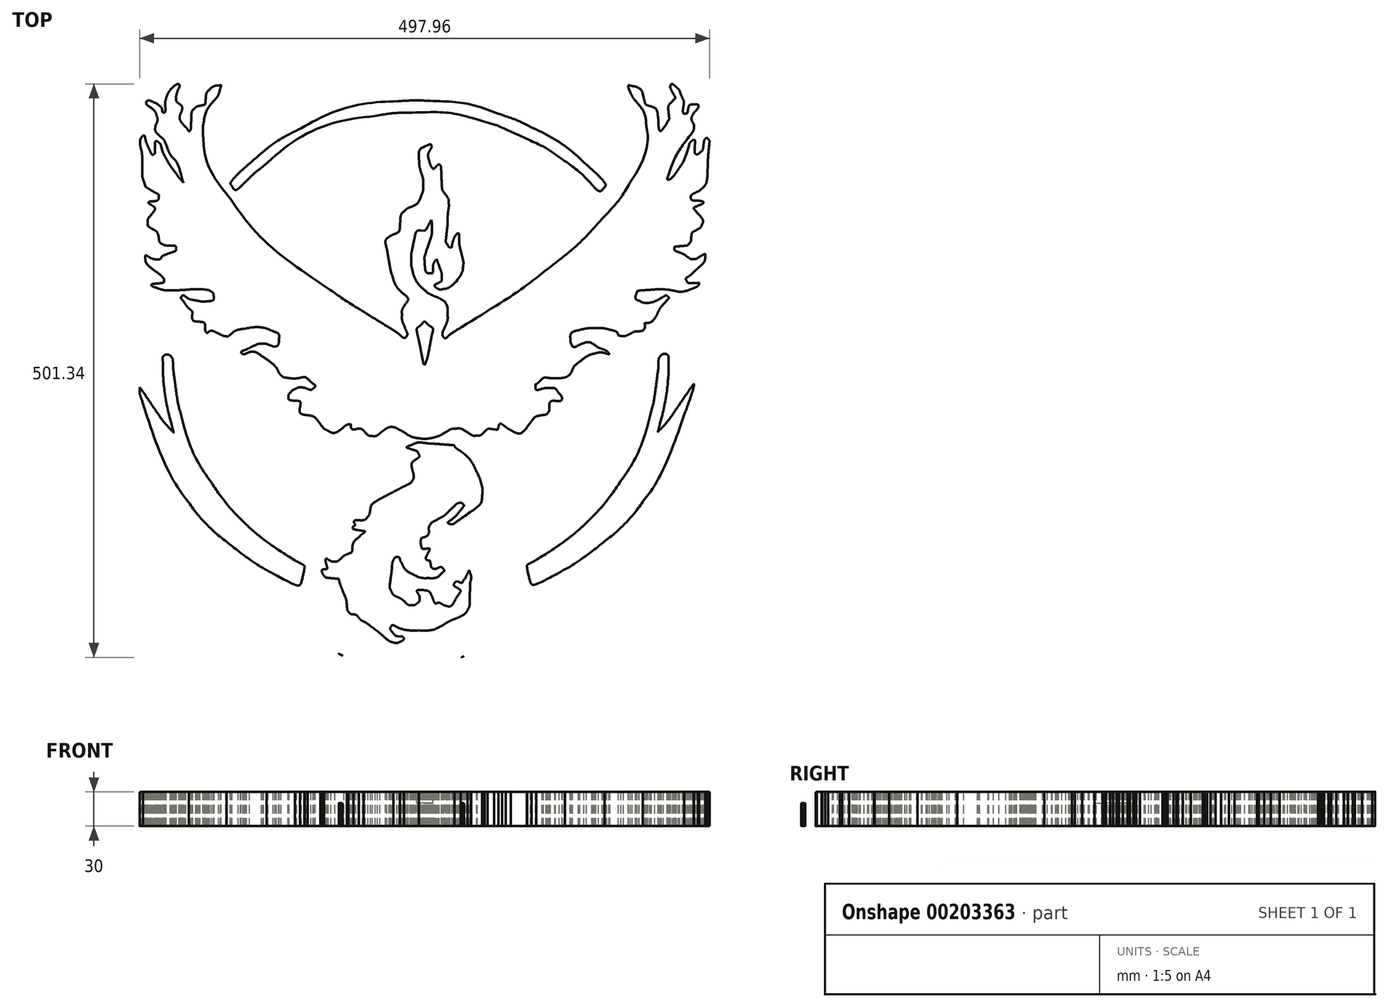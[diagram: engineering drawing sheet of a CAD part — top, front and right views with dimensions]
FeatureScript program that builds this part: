
annotation { "Feature Type Name" : "Feature", "Feature Type Description" : "" }
export const myFeature = defineFeature(function(context is Context, id is Id, definition is map)
    precondition{}
    {
        {
            var Q0;
            Q0=qCreatedBy(makeId("Top.planeOp"),FACE);
            var sketch = newSketch(context, id + "F0", { "sketchPlane" : qUnion([Q0])});
            skFitSpline(sketch, "E0", {"points": [v(217.87, 275.93) * mm, v(210.33, 275.93) * mm, v(203.9, 273.15) * mm, v(199.1, 269.63) * mm]});
            skFitSpline(sketch, "E1", {"points": [v(199.1, 269.63) * mm, v(196.14, 271.33) * mm, v(193.14, 272.64) * mm, v(190.27, 273.4) * mm]});
            skFitSpline(sketch, "E2", {"points": [v(190.27, 273.4) * mm, v(190.23, 273.4) * mm, v(190.19, 273.41) * mm, v(190.15, 273.42) * mm]});
            skFitSpline(sketch, "E3", {"points": [v(190.15, 273.42) * mm, v(188.24, 273.91) * mm, v(186.38, 274.47) * mm, v(182.33, 274.73) * mm]});
            skFitSpline(sketch, "E4", {"points": [v(182.33, 274.73) * mm, v(180.3, 274.85) * mm, v(177.7, 275.05) * mm, v(173.12, 274) * mm]});
            skFitSpline(sketch, "E5", {"points": [v(173.12, 274) * mm, v(168.53, 272.96) * mm, v(160.24, 269.98) * mm, v(154.3, 261.08) * mm]});
            skFitSpline(sketch, "E6", {"points": [v(154.3, 261.08) * mm, v(153.97, 260.58) * mm, v(153.65, 260.07) * mm, v(153.35, 259.54) * mm]});
            skFitSpline(sketch, "E7", {"points": [v(153.35, 259.54) * mm, v(145.44, 245.99) * mm, v(149.13, 243.88) * mm, v(149.3, 241.69) * mm]});
            skFitSpline(sketch, "E8", {"points": [v(149.3, 241.69) * mm, v(149.49, 239.5) * mm, v(149.72, 238.52) * mm, v(149.9, 237.7) * mm]});
            skFitSpline(sketch, "E9", {"points": [v(149.9, 237.7) * mm, v(150.24, 236.04) * mm, v(150.48, 235.27) * mm, v(150.7, 234.5) * mm]});
            skFitSpline(sketch, "E10", {"points": [v(150.7, 234.5) * mm, v(151.17, 232.95) * mm, v(151.58, 231.76) * mm, v(152.04, 230.48) * mm]});
            skFitSpline(sketch, "E11", {"points": [v(152.04, 230.48) * mm, v(152.95, 227.93) * mm, v(153.64, 225.9) * mm, v(155.43, 222.25) * mm]});
            skFitSpline(sketch, "E12", {"points": [v(155.43, 222.25) * mm, v(158.19, 216.6) * mm, v(159.29, 215.5) * mm, v(161.98, 212.21) * mm]});
            skFitSpline(sketch, "E13", {"points": [v(161.98, 212.21) * mm, v(165.62, 207.76) * mm, v(164.59, 210) * mm, v(165.02, 205.5) * mm]});
            skFitSpline(sketch, "E14", {"points": [v(165.02, 205.5) * mm, v(165.03, 205.48) * mm, v(165.03, 205.47) * mm, v(165.03, 205.45) * mm]});
            skFitSpline(sketch, "E15", {"points": [v(165.03, 205.45) * mm, v(165.05, 205.18) * mm, v(164.23, 200.38) * mm, v(162.5, 194.17) * mm]});
            skFitSpline(sketch, "E16", {"points": [v(162.5, 194.17) * mm, v(161.88, 194.74) * mm, v(161.27, 195.3) * mm, v(160.67, 195.83) * mm]});
            skLineSegment(sketch, "E17", {"start": v(160.67, 195.83) * mm, "end": v(160.66, 195.84) * mm});
            skFitSpline(sketch, "E18", {"points": [v(160.66, 195.84) * mm, v(144.48, 210.26) * mm, v(126.32, 222.5) * mm, v(106.6, 232.38) * mm]});
            skFitSpline(sketch, "E19", {"points": [v(106.6, 232.38) * mm, v(106.6, 232.39) * mm, v(106.59, 232.4) * mm, v(106.58, 232.4) * mm]});
            skFitSpline(sketch, "E20", {"points": [v(106.58, 232.4) * mm, v(96.35, 237.52) * mm, v(88.61, 240.69) * mm, v(74.93, 245.48) * mm]});
            skFitSpline(sketch, "E21", {"points": [v(74.93, 245.48) * mm, v(74.92, 245.48) * mm, v(74.91, 245.49) * mm, v(74.9, 245.5) * mm]});
            skFitSpline(sketch, "E22", {"points": [v(74.9, 245.5) * mm, v(53.44, 252.98) * mm, v(32.18, 256.93) * mm, v(7.67, 258.12) * mm]});
            skFitSpline(sketch, "E23", {"points": [v(7.67, 258.12) * mm, v(7.65, 258.13) * mm, v(7.63, 258.13) * mm, v(7.6, 258.13) * mm]});
            skFitSpline(sketch, "E24", {"points": [v(7.6, 258.13) * mm, v(5.3, 258.23) * mm, v(2.83, 258.3) * mm, v(0.2, 258.32) * mm]});
            skFitSpline(sketch, "E25", {"points": [v(0.2, 258.32) * mm, v(-7.68, 258.4) * mm, v(-16.55, 258.27) * mm, v(-23.41, 257.78) * mm]});
            skLineSegment(sketch, "E26", {"start": v(-23.41, 257.78) * mm, "end": v(-23.43, 257.77) * mm});
            skFitSpline(sketch, "E27", {"points": [v(-23.43, 257.77) * mm, v(-56.56, 255.36) * mm, v(-89.54, 246.17) * mm, v(-118.8, 231.18) * mm]});
            skLineSegment(sketch, "E28", {"start": v(-118.8, 231.18) * mm, "end": v(-118.8, 231.17) * mm});
            skFitSpline(sketch, "E29", {"points": [v(-118.8, 231.17) * mm, v(-133.83, 223.46) * mm, v(-147.06, 214.76) * mm, v(-161.5, 203.13) * mm]});
            skFitSpline(sketch, "E30", {"points": [v(-161.5, 203.13) * mm, v(-161.4, 204.67) * mm, v(-161.33, 207.22) * mm, v(-161.45, 207.37) * mm]});
            skFitSpline(sketch, "E31", {"points": [v(-161.45, 207.37) * mm, v(-161.13, 208.45) * mm, v(-160.13, 210.7) * mm, v(-158.87, 212.2) * mm]});
            skLineSegment(sketch, "E32", {"start": v(-158.87, 212.2) * mm, "end": v(-159.02, 212.01) * mm});
            skFitSpline(sketch, "E33", {"points": [v(-159.02, 212.01) * mm, v(-154.46, 217.33) * mm, v(-149.72, 226.82) * mm, v(-147.9, 233.25) * mm]});
            skLineSegment(sketch, "E34", {"start": v(-147.9, 233.25) * mm, "end": v(-147.96, 233.06) * mm});
            skFitSpline(sketch, "E35", {"points": [v(-147.96, 233.06) * mm, v(-147.66, 234.1) * mm, v(-147.23, 235.27) * mm, v(-146.73, 238.35) * mm]});
            skFitSpline(sketch, "E36", {"points": [v(-146.73, 238.35) * mm, v(-146.23, 241.42) * mm, v(-144.3, 248.07) * mm, v(-150.13, 258.68) * mm]});
            skFitSpline(sketch, "E37", {"points": [v(-150.13, 258.68) * mm, v(-155.95, 269.3) * mm, v(-168.74, 273.93) * mm, v(-173.7, 274.53) * mm]});
            skFitSpline(sketch, "E38", {"points": [v(-173.7, 274.53) * mm, v(-178.67, 275.13) * mm, v(-180.16, 274.7) * mm, v(-181.26, 274.6) * mm]});
            skLineSegment(sketch, "E39", {"start": v(-181.26, 274.6) * mm, "end": v(-181.03, 274.63) * mm});
            skFitSpline(sketch, "E40", {"points": [v(-181.03, 274.63) * mm, v(-188.08, 274.08) * mm, v(-192.97, 272.73) * mm, v(-197.12, 270.53) * mm]});
            skFitSpline(sketch, "E41", {"points": [v(-197.12, 270.53) * mm, v(-198.09, 271.18) * mm, v(-199.07, 271.78) * mm, v(-200.1, 272.3) * mm]});
            skFitSpline(sketch, "E42", {"points": [v(-200.1, 272.3) * mm, v(-210.4, 277.41) * mm, v(-221.7, 276.07) * mm, v(-229.74, 271.82) * mm]});
            skFitSpline(sketch, "E43", {"points": [v(-229.74, 271.82) * mm, v(-229.8, 271.78) * mm, v(-229.87, 271.75) * mm, v(-229.93, 271.72) * mm]});
            skFitSpline(sketch, "E44", {"points": [v(-229.93, 271.72) * mm, v(-238.87, 266.9) * mm, v(-236.88, 266.92) * mm, v(-238.75, 265.23) * mm]});
            skFitSpline(sketch, "E45", {"points": [v(-238.75, 265.23) * mm, v(-240.22, 263.9) * mm, v(-240.43, 264.86) * mm, v(-243.28, 261.1) * mm]});
            skFitSpline(sketch, "E46", {"points": [v(-243.28, 261.1) * mm, v(-249.02, 260.28) * mm, v(-254.1, 257.93) * mm, v(-258.33, 254.82) * mm]});
            skFitSpline(sketch, "E47", {"points": [v(-258.33, 254.82) * mm, v(-266.03, 249.14) * mm, v(-274.63, 236.82) * mm, v(-270.76, 221.05) * mm]});
            skFitSpline(sketch, "E48", {"points": [v(-270.76, 221.05) * mm, v(-270.7, 220.86) * mm, v(-270.66, 220.66) * mm, v(-270.6, 220.47) * mm]});
            skFitSpline(sketch, "E49", {"points": [v(-270.6, 220.47) * mm, v(-270.33, 219.42) * mm, v(-270.04, 218.5) * mm, v(-269.76, 217.62) * mm]});
            skFitSpline(sketch, "E50", {"points": [v(-269.76, 217.62) * mm, v(-270.53, 216.6) * mm, v(-271.32, 215.43) * mm, v(-272.15, 214.06) * mm]});
            skFitSpline(sketch, "E51", {"points": [v(-272.15, 214.06) * mm, v(-272.16, 214.04) * mm, v(-272.17, 214.03) * mm, v(-272.18, 214) * mm]});
            skFitSpline(sketch, "E52", {"points": [v(-272.18, 214) * mm, v(-273.24, 212.26) * mm, v(-276, 206.15) * mm, v(-276.7, 201.8) * mm]});
            skFitSpline(sketch, "E53", {"points": [v(-276.7, 201.8) * mm, v(-277.38, 197.68) * mm, v(-277.22, 195.9) * mm, v(-277.2, 194.35) * mm]});
            skFitSpline(sketch, "E54", {"points": [v(-277.2, 194.35) * mm, v(-277.2, 190.35) * mm, v(-277.76, 189.7) * mm, v(-275.74, 182.22) * mm]});
            skFitSpline(sketch, "E55", {"points": [v(-275.74, 182.22) * mm, v(-275.35, 180.83) * mm, v(-275.57, 182.83) * mm, v(-275.52, 174.9) * mm]});
            skFitSpline(sketch, "E56", {"points": [v(-275.52, 174.9) * mm, v(-275.52, 174.9) * mm, v(-275.52, 174.9) * mm, v(-275.52, 174.9) * mm]});
            skFitSpline(sketch, "E57", {"points": [v(-275.52, 174.9) * mm, v(-275.47, 165) * mm, v(-273.97, 155.5) * mm, v(-271.7, 148.63) * mm]});
            skFitSpline(sketch, "E58", {"points": [v(-271.7, 148.63) * mm, v(-271.7, 148.62) * mm, v(-271.69, 148.6) * mm, v(-271.68, 148.59) * mm]});
            skLineSegment(sketch, "E59", {"start": v(-271.68, 148.59) * mm, "end": v(-270.9, 146.22) * mm});
            skFitSpline(sketch, "E60", {"points": [v(-270.9, 146.22) * mm, v(-270.55, 145.2) * mm, v(-270.15, 144.2) * mm, v(-269.7, 143.21) * mm]});
            skFitSpline(sketch, "E61", {"points": [v(-269.7, 143.21) * mm, v(-269.7, 142.96) * mm, v(-269.75, 142.7) * mm, v(-269.76, 142.45) * mm]});
            skFitSpline(sketch, "E62", {"points": [v(-269.76, 142.45) * mm, v(-269.78, 139.72) * mm, v(-269.44, 137.28) * mm, v(-268.92, 135.06) * mm]});
            skFitSpline(sketch, "E63", {"points": [v(-268.92, 135.06) * mm, v(-269.93, 131.8) * mm, v(-270.61, 128.35) * mm, v(-270.61, 124.93) * mm]});
            skFitSpline(sketch, "E64", {"points": [v(-270.61, 124.93) * mm, v(-270.61, 121.34) * mm, v(-269.53, 116.12) * mm, v(-267.6, 111.19) * mm]});
            skFitSpline(sketch, "E65", {"points": [v(-267.6, 111.19) * mm, v(-270.75, 106.2) * mm, v(-272, 101.24) * mm, v(-272.4, 98.4) * mm]});
            skFitSpline(sketch, "E66", {"points": [v(-272.4, 98.4) * mm, v(-273.06, 93.69) * mm, v(-272.73, 91.52) * mm, v(-272.57, 89.72) * mm]});
            skFitSpline(sketch, "E67", {"points": [v(-272.57, 89.72) * mm, v(-272.46, 88.32) * mm, v(-272.53, 86.77) * mm, v(-271.34, 82.44) * mm]});
            skFitSpline(sketch, "E68", {"points": [v(-271.34, 82.44) * mm, v(-271.15, 81.75) * mm, v(-270.82, 80.9) * mm, v(-270.43, 79.97) * mm]});
            skFitSpline(sketch, "E69", {"points": [v(-270.43, 79.97) * mm, v(-270.58, 80.56) * mm, v(-270.71, 81.2) * mm, v(-270.84, 81.87) * mm]});
            skFitSpline(sketch, "E70", {"points": [v(-270.84, 81.87) * mm, v(-270.67, 81.04) * mm, v(-270.49, 80.3) * mm, v(-270.28, 79.64) * mm]});
            skFitSpline(sketch, "E71", {"points": [v(-270.28, 79.64) * mm, v(-269.43, 77.72) * mm, v(-268.23, 75.47) * mm, v(-266.65, 73.17) * mm]});
            skFitSpline(sketch, "E72", {"points": [v(-266.65, 73.17) * mm, v(-266.67, 73.06) * mm, v(-266.7, 72.94) * mm, v(-266.71, 72.82) * mm]});
            skFitSpline(sketch, "E73", {"points": [v(-266.71, 72.82) * mm, v(-266.3, 72.18) * mm, v(-265.94, 71.61) * mm, v(-265.64, 71.2) * mm]});
            skFitSpline(sketch, "E74", {"points": [v(-265.64, 71.2) * mm, v(-266.01, 71.6) * mm, v(-266.34, 71.97) * mm, v(-266.76, 72.47) * mm]});
            skFitSpline(sketch, "E75", {"points": [v(-266.76, 72.47) * mm, v(-267.02, 70.24) * mm, v(-267.04, 68.13) * mm, v(-266.78, 66.3) * mm]});
            skFitSpline(sketch, "E76", {"points": [v(-266.78, 66.3) * mm, v(-265.72, 58.82) * mm, v(-263.1, 55.2) * mm, v(-261.37, 52.78) * mm]});
            skFitSpline(sketch, "E77", {"points": [v(-261.37, 52.78) * mm, v(-257.92, 47.93) * mm, v(-256.07, 46.94) * mm, v(-254.59, 45.8) * mm]});
            skFitSpline(sketch, "E78", {"points": [v(-254.59, 45.8) * mm, v(-251.62, 43.52) * mm, v(-249.98, 42.7) * mm, v(-248.16, 41.75) * mm]});
            skFitSpline(sketch, "E79", {"points": [v(-248.16, 41.75) * mm, v(-245.76, 40.47) * mm, v(-243.56, 39.39) * mm, v(-240.8, 38.37) * mm]});
            skFitSpline(sketch, "E80", {"points": [v(-240.8, 38.37) * mm, v(-243.17, 37.13) * mm, v(-245.64, 35.49) * mm, v(-248.19, 33.3) * mm]});
            skLineSegment(sketch, "E81", {"start": v(-248.19, 33.3) * mm, "end": v(-248.98, 32.63) * mm});
            skFitSpline(sketch, "E82", {"points": [v(-248.98, 32.63) * mm, v(-255.3, 27.19) * mm, v(-259.37, 19.58) * mm, v(-260.38, 11.3) * mm]});
            skFitSpline(sketch, "E83", {"points": [v(-260.38, 11.3) * mm, v(-272.63, 6.13) * mm, v(-280.65, -5.81) * mm, v(-280.82, -19.11) * mm]});
            skLineSegment(sketch, "E84", {"start": v(-280.82, -19.11) * mm, "end": v(-280.84, -21.46) * mm});
            skFitSpline(sketch, "E85", {"points": [v(-280.84, -21.46) * mm, v(-280.84, -21.59) * mm, v(-280.85, -21.72) * mm, v(-280.85, -21.86) * mm]});
            skFitSpline(sketch, "E86", {"points": [v(-280.85, -21.86) * mm, v(-280.85, -24.72) * mm, v(-280.29, -30.22) * mm, v(-279.37, -33.94) * mm]});
            skFitSpline(sketch, "E87", {"points": [v(-279.37, -33.94) * mm, v(-278.45, -37.67) * mm, v(-277.52, -40.33) * mm, v(-276.2, -44.28) * mm]});
            skFitSpline(sketch, "E88", {"points": [v(-276.2, -44.28) * mm, v(-276.19, -44.3) * mm, v(-276.18, -44.33) * mm, v(-276.17, -44.35) * mm]});
            skFitSpline(sketch, "E89", {"points": [v(-276.17, -44.35) * mm, v(-263.73, -81.15) * mm, v(-248.31, -116.35) * mm, v(-231.6, -139.58) * mm]});
            skFitSpline(sketch, "E90", {"points": [v(-231.6, -139.58) * mm, v(-231.6, -139.59) * mm, v(-231.6, -139.59) * mm, v(-231.6, -139.59) * mm]});
            skFitSpline(sketch, "E91", {"points": [v(-231.6, -139.59) * mm, v(-231.59, -139.6) * mm, v(-231.59, -139.6) * mm, v(-231.59, -139.6) * mm]});
            skFitSpline(sketch, "E92", {"points": [v(-231.59, -139.6) * mm, v(-221.07, -154.22) * mm, v(-206.57, -169.11) * mm, v(-192.24, -180.57) * mm]});
            skFitSpline(sketch, "E93", {"points": [v(-192.24, -180.57) * mm, v(-180.15, -190.28) * mm, v(-165.88, -201.17) * mm, v(-152.64, -208.47) * mm]});
            skFitSpline(sketch, "E94", {"points": [v(-152.64, -208.47) * mm, v(-147.53, -211.3) * mm, v(-141.76, -214.36) * mm, v(-136.76, -216.94) * mm]});
            skFitSpline(sketch, "E95", {"points": [v(-136.76, -216.94) * mm, v(-131.75, -219.52) * mm, v(-131.21, -220.35) * mm, v(-123.5, -223.28) * mm]});
            skFitSpline(sketch, "E96", {"points": [v(-123.5, -223.28) * mm, v(-123.3, -223.35) * mm, v(-123.09, -223.43) * mm, v(-122.88, -223.5) * mm]});
            skFitSpline(sketch, "E97", {"points": [v(-122.88, -223.5) * mm, v(-117.12, -225.56) * mm, v(-113.06, -226) * mm, v(-107.92, -225.81) * mm]});
            skFitSpline(sketch, "E98", {"points": [v(-107.92, -225.81) * mm, v(-105.13, -225.72) * mm, v(-101.73, -226.74) * mm, v(-97.05, -225.24) * mm]});
            skFitSpline(sketch, "E99", {"points": [v(-97.05, -225.24) * mm, v(-95.61, -228.87) * mm, v(-93.44, -232.84) * mm, v(-92.3, -234.5) * mm]});
            skFitSpline(sketch, "E100", {"points": [v(-92.3, -234.5) * mm, v(-88, -240.63) * mm, v(-81.93, -245.22) * mm, v(-75.36, -248.02) * mm]});
            skFitSpline(sketch, "E101", {"points": [v(-75.36, -248.02) * mm, v(-72.71, -250.18) * mm, v(-69.9, -252.2) * mm, v(-67.81, -253.33) * mm]});
            skLineSegment(sketch, "E102", {"start": v(-67.81, -253.33) * mm, "end": v(-68.16, -253.13) * mm});
            skFitSpline(sketch, "E103", {"points": [v(-68.16, -253.13) * mm, v(-71.04, -251.52) * mm, v(-67, -253.96) * mm, v(-64.22, -256.03) * mm]});
            skFitSpline(sketch, "E104", {"points": [v(-64.22, -256.03) * mm, v(-61.44, -258.1) * mm, v(-58.17, -260.68) * mm, v(-56.25, -262.3) * mm]});
            skFitSpline(sketch, "E105", {"points": [v(-56.25, -262.3) * mm, v(-56.22, -262.33) * mm, v(-56.2, -262.35) * mm, v(-56.17, -262.37) * mm]});
            skFitSpline(sketch, "E106", {"points": [v(-56.17, -262.37) * mm, v(-50.78, -266.9) * mm, v(-44.46, -271.73) * mm, v(-35, -274.45) * mm]});
            skFitSpline(sketch, "E107", {"points": [v(-35, -274.45) * mm, v(-34.87, -274.49) * mm, v(-34.75, -274.52) * mm, v(-34.63, -274.55) * mm]});
            skFitSpline(sketch, "E108", {"points": [v(-34.63, -274.55) * mm, v(-25.12, -277.17) * mm, v(-13.96, -275.95) * mm, v(-5.5, -271.85) * mm]});
            skFitSpline(sketch, "E109", {"points": [v(-5.5, -271.85) * mm, v(-5.47, -271.83) * mm, v(-5.43, -271.82) * mm, v(-5.4, -271.8) * mm]});
            skFitSpline(sketch, "E110", {"points": [v(-5.4, -271.8) * mm, v(-2.1, -270.2) * mm, v(1.53, -268.22) * mm, v(5.15, -264.63) * mm]});
            skFitSpline(sketch, "E111", {"points": [v(5.15, -264.63) * mm, v(16.55, -263.22) * mm, v(28.3, -259.27) * mm, v(37.99, -253.78) * mm]});
            skFitSpline(sketch, "E112", {"points": [v(37.99, -253.78) * mm, v(38.05, -253.75) * mm, v(38.1, -253.72) * mm, v(38.16, -253.69) * mm]});
            skFitSpline(sketch, "E113", {"points": [v(38.16, -253.69) * mm, v(36.19, -254.82) * mm, v(39.56, -253.09) * mm, v(39.86, -252.97) * mm]});
            skFitSpline(sketch, "E114", {"points": [v(39.86, -252.97) * mm, v(39.94, -252.94) * mm, v(40.01, -252.9) * mm, v(40.09, -252.88) * mm]});
            skFitSpline(sketch, "E115", {"points": [v(40.09, -252.88) * mm, v(42.8, -251.78) * mm, v(44.12, -251.38) * mm, v(48.26, -249.25) * mm]});
            skFitSpline(sketch, "E116", {"points": [v(48.26, -249.25) * mm, v(48.43, -249.16) * mm, v(48.6, -249.07) * mm, v(48.77, -248.98) * mm]});
            skFitSpline(sketch, "E117", {"points": [v(48.77, -248.98) * mm, v(59.28, -243.33) * mm, v(61.39, -243.75) * mm, v(68.93, -228.65) * mm]});
            skFitSpline(sketch, "E118", {"points": [v(68.93, -228.65) * mm, v(68.95, -228.61) * mm, v(68.97, -228.58) * mm, v(68.99, -228.54) * mm]});
            skFitSpline(sketch, "E119", {"points": [v(68.99, -228.54) * mm, v(69.56, -227.39) * mm, v(70.4, -225.32) * mm, v(71.21, -222.93) * mm]});
            skFitSpline(sketch, "E120", {"points": [v(71.21, -222.93) * mm, v(82.19, -232.42) * mm, v(89.6, -230.78) * mm, v(95, -231) * mm]});
            skFitSpline(sketch, "E121", {"points": [v(95, -231) * mm, v(101.2, -231.25) * mm, v(106.18, -230.53) * mm, v(112.23, -228.38) * mm]});
            skFitSpline(sketch, "E122", {"points": [v(112.23, -228.38) * mm, v(122.6, -224.7) * mm, v(121.63, -224.23) * mm, v(126.71, -221.62) * mm]});
            skFitSpline(sketch, "E123", {"points": [v(126.71, -221.62) * mm, v(131.78, -219.02) * mm, v(137.62, -215.92) * mm, v(142.99, -212.93) * mm]});
            skFitSpline(sketch, "E124", {"points": [v(142.99, -212.93) * mm, v(157.44, -204.97) * mm, v(170.99, -194.47) * mm, v(183.37, -184.52) * mm]});
            skLineSegment(sketch, "E125", {"start": v(183.37, -184.52) * mm, "end": v(183.38, -184.51) * mm});
            skFitSpline(sketch, "E126", {"points": [v(183.38, -184.51) * mm, v(198.33, -172.57) * mm, v(212.77, -157.77) * mm, v(223.83, -142.38) * mm]});
            skLineSegment(sketch, "E127", {"start": v(223.83, -142.38) * mm, "end": v(223.83, -142.37) * mm});
            skFitSpline(sketch, "E128", {"points": [v(223.83, -142.37) * mm, v(239.27, -120.92) * mm, v(252.53, -91.56) * mm, v(265.2, -56.84) * mm]});
            skFitSpline(sketch, "E129", {"points": [v(265.2, -56.84) * mm, v(266.9, -52.25) * mm, v(268.81, -46.69) * mm, v(270.5, -41.64) * mm]});
            skFitSpline(sketch, "E130", {"points": [v(270.5, -41.64) * mm, v(272.18, -36.6) * mm, v(272.84, -35.82) * mm, v(274.65, -28.1) * mm]});
            skFitSpline(sketch, "E131", {"points": [v(274.65, -28.1) * mm, v(275.08, -26.25) * mm, v(275.57, -24.23) * mm, v(275.82, -20.38) * mm]});
            skFitSpline(sketch, "E132", {"points": [v(275.82, -20.38) * mm, v(276.06, -16.52) * mm, v(279.73, -10.63) * mm, v(268.82, 5.1) * mm]});
            skFitSpline(sketch, "E133", {"points": [v(268.82, 5.1) * mm, v(265.57, 9.79) * mm, v(259.42, 14.66) * mm, v(252.6, 17.97) * mm]});
            skFitSpline(sketch, "E134", {"points": [v(252.6, 17.97) * mm, v(250.66, 25.14) * mm, v(246.73, 31.6) * mm, v(241.27, 36.63) * mm]});
            skFitSpline(sketch, "E135", {"points": [v(241.27, 36.63) * mm, v(243.76, 37.45) * mm, v(244.12, 38.02) * mm, v(246.2, 38.87) * mm]});
            skFitSpline(sketch, "E136", {"points": [v(246.2, 38.87) * mm, v(247.84, 39.54) * mm, v(249.4, 40.2) * mm, v(250.98, 40.92) * mm]});
            skFitSpline(sketch, "E137", {"points": [v(250.98, 40.92) * mm, v(251.77, 41.28) * mm, v(252.54, 41.63) * mm, v(253.6, 42.18) * mm]});
            skFitSpline(sketch, "E138", {"points": [v(253.6, 42.18) * mm, v(254.65, 42.73) * mm, v(254.5, 41.5) * mm, v(260.54, 46.9) * mm]});
            skFitSpline(sketch, "E139", {"points": [v(260.54, 46.9) * mm, v(260.63, 46.97) * mm, v(260.7, 47.05) * mm, v(260.8, 47.12) * mm]});
            skFitSpline(sketch, "E140", {"points": [v(260.8, 47.12) * mm, v(272, 57.35) * mm, v(270.53, 62) * mm, v(271.1, 68.08) * mm]});
            skFitSpline(sketch, "E141", {"points": [v(271.1, 68.08) * mm, v(271.3, 70.16) * mm, v(271.7, 72.28) * mm, v(271.07, 75.85) * mm]});
            skFitSpline(sketch, "E142", {"points": [v(271.07, 75.85) * mm, v(273.94, 80.9) * mm, v(276.16, 86.45) * mm, v(276.77, 91.59) * mm]});
            skFitSpline(sketch, "E143", {"points": [v(276.77, 91.59) * mm, v(276.8, 91.75) * mm, v(276.81, 91.91) * mm, v(276.83, 92.08) * mm]});
            skFitSpline(sketch, "E144", {"points": [v(276.83, 92.08) * mm, v(276.95, 93.26) * mm, v(277.5, 94.24) * mm, v(276.87, 99.91) * mm]});
            skFitSpline(sketch, "E145", {"points": [v(276.87, 99.91) * mm, v(276.56, 102.68) * mm, v(275.88, 107.27) * mm, v(272.37, 112.9) * mm]});
            skFitSpline(sketch, "E146", {"points": [v(272.37, 112.9) * mm, v(274.35, 118.62) * mm, v(274.75, 126.19) * mm, v(273.6, 132.52) * mm]});
            skFitSpline(sketch, "E147", {"points": [v(273.6, 132.52) * mm, v(274.65, 135.5) * mm, v(275.48, 139.34) * mm, v(275.2, 144.23) * mm]});
            skFitSpline(sketch, "E148", {"points": [v(275.2, 144.23) * mm, v(275.14, 145.24) * mm, v(274.99, 146.29) * mm, v(274.8, 147.35) * mm]});
            skFitSpline(sketch, "E149", {"points": [v(274.8, 147.35) * mm, v(276.38, 150.78) * mm, v(277.6, 154.34) * mm, v(278.1, 157.63) * mm]});
            skFitSpline(sketch, "E150", {"points": [v(278.1, 157.63) * mm, v(278.87, 162.38) * mm, v(278.6, 162.25) * mm, v(278.73, 164.32) * mm]});
            skFitSpline(sketch, "E151", {"points": [v(278.73, 164.32) * mm, v(278.85, 166.43) * mm, v(278.96, 168.85) * mm, v(279.05, 171.29) * mm]});
            skLineSegment(sketch, "E152", {"start": v(279.05, 171.29) * mm, "end": v(279.05, 171.32) * mm});
            skFitSpline(sketch, "E153", {"points": [v(279.05, 171.32) * mm, v(279.32, 178.6) * mm, v(279.64, 183.28) * mm, v(280.33, 189.62) * mm]});
            skLineSegment(sketch, "E154", {"start": v(280.33, 189.62) * mm, "end": v(280.33, 189.64) * mm});
            skLineSegment(sketch, "E155", {"start": v(280.33, 189.64) * mm, "end": v(280.66, 192.55) * mm});
            skFitSpline(sketch, "E156", {"points": [v(280.66, 192.55) * mm, v(281.56, 200.55) * mm, v(279.23, 208.58) * mm, v(274.2, 214.87) * mm]});
            skLineSegment(sketch, "E157", {"start": v(274.2, 214.87) * mm, "end": v(273.35, 215.93) * mm});
            skLineSegment(sketch, "E158", {"start": v(273.35, 215.93) * mm, "end": v(273.35, 215.93) * mm});
            skFitSpline(sketch, "E159", {"points": [v(273.35, 215.93) * mm, v(272.58, 216.9) * mm, v(271.7, 218.21) * mm, v(270.34, 219.66) * mm]});
            skFitSpline(sketch, "E160", {"points": [v(270.34, 219.66) * mm, v(270.67, 221.55) * mm, v(270.89, 223.76) * mm, v(270.89, 226.44) * mm]});
            skFitSpline(sketch, "E161", {"points": [v(270.89, 226.44) * mm, v(270.89, 236.75) * mm, v(260.56, 251.29) * mm, v(252.7, 254.97) * mm]});
            skFitSpline(sketch, "E162", {"points": [v(252.7, 254.97) * mm, v(251.6, 255.48) * mm, v(250.6, 255.9) * mm, v(249.64, 256.26) * mm]});
            skFitSpline(sketch, "E163", {"points": [v(249.64, 256.26) * mm, v(249, 257.32) * mm, v(248.3, 258.38) * mm, v(247.54, 259.38) * mm]});
            skFitSpline(sketch, "E164", {"points": [v(247.54, 259.38) * mm, v(244.54, 263.26) * mm, v(242.81, 264.5) * mm, v(241.43, 265.74) * mm]});
            skLineSegment(sketch, "E165", {"start": v(241.43, 265.74) * mm, "end": v(241.63, 265.56) * mm});
            skFitSpline(sketch, "E166", {"points": [v(241.63, 265.56) * mm, v(240.23, 266.84) * mm, v(238.9, 268) * mm, v(236.95, 269.43) * mm]});
            skFitSpline(sketch, "E167", {"points": [v(236.95, 269.43) * mm, v(235.98, 270.14) * mm, v(234.9, 270.93) * mm, v(232.88, 272.04) * mm]});
            skFitSpline(sketch, "E168", {"points": [v(232.88, 272.04) * mm, v(230.84, 273.15) * mm, v(229.5, 275.93) * mm, v(217.87, 275.93) * mm]});
            skLineSegment(sketch, "E169", {"start": v(217.87, 275.93) * mm, "end": v(217.87, 275.93) * mm});
            skFitSpline(sketch, "E170", {"points": [v(-109.28, -191.27) * mm, v(-111.73, -190.34) * mm, v(-124.68, -183.68) * mm, v(-134.11, -178.46) * mm]});
            skFitSpline(sketch, "E171", {"points": [v(-134.11, -178.46) * mm, v(-140.2, -175.1) * mm, v(-158.64, -162.03) * mm, v(-168.97, -153.73) * mm]});
            skFitSpline(sketch, "E172", {"points": [v(-168.97, -153.73) * mm, v(-179.77, -145.1) * mm, v(-194.7, -129.58) * mm, v(-202.07, -119.33) * mm]});
            skFitSpline(sketch, "E173", {"points": [v(-202.07, -119.33) * mm, v(-214.18, -102.51) * mm, v(-230.49, -67.29) * mm, v(-242.12, -32.92) * mm]});
            skFitSpline(sketch, "E174", {"points": [v(-242.12, -32.92) * mm, v(-244.66, -25.35) * mm, v(-245.02, -23.86) * mm, v(-245.02, -21.15) * mm]});
            skLineSegment(sketch, "E175", {"start": v(-245.02, -21.15) * mm, "end": v(-245, -18.8) * mm});
            skLineSegment(sketch, "E176", {"start": v(-245, -18.8) * mm, "end": v(-244.32, -19.65) * mm});
            skFitSpline(sketch, "E177", {"points": [v(-244.32, -19.65) * mm, v(-243.64, -20.44) * mm, v(-241.9, -22.98) * mm, v(-232.8, -36.3) * mm]});
            skFitSpline(sketch, "E178", {"points": [v(-232.8, -36.3) * mm, v(-226.65, -45.3) * mm, v(-221.88, -51.4) * mm, v(-217.23, -56.34) * mm]});
            skFitSpline(sketch, "E179", {"points": [v(-217.23, -56.34) * mm, v(-215.79, -57.86) * mm, v(-215.4, -58.15) * mm, v(-215.53, -57.6) * mm]});
            skFitSpline(sketch, "E180", {"points": [v(-215.53, -57.6) * mm, v(-215.62, -57.21) * mm, v(-216.32, -54.45) * mm, v(-217.08, -51.46) * mm]});
            skFitSpline(sketch, "E181", {"points": [v(-217.08, -51.46) * mm, v(-220.27, -38.98) * mm, v(-223.3, -22.02) * mm, v(-224.45, -9.91) * mm]});
            skFitSpline(sketch, "E182", {"points": [v(-224.45, -9.91) * mm, v(-224.65, -7.97) * mm, v(-224.82, -3.17) * mm, v(-224.82, 0.75) * mm]});
            skLineSegment(sketch, "E183", {"start": v(-224.82, 0.75) * mm, "end": v(-224.85, 7.92) * mm});
            skLineSegment(sketch, "E184", {"start": v(-224.85, 7.92) * mm, "end": v(-224.06, 8.6) * mm});
            skFitSpline(sketch, "E185", {"points": [v(-224.06, 8.6) * mm, v(-222.47, 9.95) * mm, v(-218.6, 9.3) * mm, v(-217.14, 7.44) * mm]});
            skFitSpline(sketch, "E186", {"points": [v(-217.14, 7.44) * mm, v(-216.24, 6.31) * mm, v(-216.01, 5.21) * mm, v(-215.84, 1.1) * mm]});
            skFitSpline(sketch, "E187", {"points": [v(-215.84, 1.1) * mm, v(-215.64, -3.28) * mm, v(-215.48, -4.72) * mm, v(-213.95, -16.18) * mm]});
            skFitSpline(sketch, "E188", {"points": [v(-213.95, -16.18) * mm, v(-212.31, -28.4) * mm, v(-211.04, -35) * mm, v(-208.45, -44.26) * mm]});
            skFitSpline(sketch, "E189", {"points": [v(-208.45, -44.26) * mm, v(-202.92, -64.21) * mm, v(-193.4, -85.38) * mm, v(-182.85, -101.21) * mm]});
            skFitSpline(sketch, "E190", {"points": [v(-182.85, -101.21) * mm, v(-175.85, -111.68) * mm, v(-164.7, -125.7) * mm, v(-157.4, -133.22) * mm]});
            skFitSpline(sketch, "E191", {"points": [v(-157.4, -133.22) * mm, v(-153.67, -137.06) * mm, v(-143.48, -146.26) * mm, v(-138.63, -150.15) * mm]});
            skFitSpline(sketch, "E192", {"points": [v(-138.63, -150.15) * mm, v(-137.16, -151.36) * mm, v(-134.68, -153.23) * mm, v(-133.12, -154.33) * mm]});
            skFitSpline(sketch, "E193", {"points": [v(-133.12, -154.33) * mm, v(-125.4, -159.75) * mm, v(-109.39, -170.02) * mm, v(-104.36, -172.76) * mm]});
            skFitSpline(sketch, "E194", {"points": [v(-104.36, -172.76) * mm, v(-101.68, -174.22) * mm, v(-100.98, -175.16) * mm, v(-101.23, -176.99) * mm]});
            skFitSpline(sketch, "E195", {"points": [v(-101.23, -176.99) * mm, v(-101.54, -179.59) * mm, v(-104.4, -190.54) * mm, v(-104.9, -191.1) * mm]});
            skFitSpline(sketch, "E196", {"points": [v(-104.9, -191.1) * mm, v(-105.5, -191.78) * mm, v(-107.7, -191.83) * mm, v(-109.28, -191.27) * mm]});
            skFitSpline(sketch, "E197", {"points": [v(97.17, -190.54) * mm, v(96.66, -189.97) * mm, v(93.81, -179.02) * mm, v(93.5, -176.43) * mm]});
            skFitSpline(sketch, "E198", {"points": [v(93.5, -176.43) * mm, v(93.25, -174.6) * mm, v(93.95, -173.66) * mm, v(96.63, -172.2) * mm]});
            skFitSpline(sketch, "E199", {"points": [v(96.63, -172.2) * mm, v(101.66, -169.45) * mm, v(117.66, -159.18) * mm, v(125.4, -153.76) * mm]});
            skFitSpline(sketch, "E200", {"points": [v(125.4, -153.76) * mm, v(126.94, -152.66) * mm, v(129.43, -150.8) * mm, v(130.9, -149.59) * mm]});
            skFitSpline(sketch, "E201", {"points": [v(130.9, -149.59) * mm, v(135.75, -145.7) * mm, v(145.94, -136.5) * mm, v(149.66, -132.65) * mm]});
            skFitSpline(sketch, "E202", {"points": [v(149.66, -132.65) * mm, v(156.97, -125.15) * mm, v(168.12, -111.12) * mm, v(175.12, -100.65) * mm]});
            skFitSpline(sketch, "E203", {"points": [v(175.12, -100.65) * mm, v(185.68, -84.82) * mm, v(195.19, -63.65) * mm, v(200.72, -43.7) * mm]});
            skFitSpline(sketch, "E204", {"points": [v(200.72, -43.7) * mm, v(203.31, -34.44) * mm, v(204.58, -27.84) * mm, v(206.22, -15.61) * mm]});
            skFitSpline(sketch, "E205", {"points": [v(206.22, -15.61) * mm, v(207.74, -4.16) * mm, v(207.91, -2.72) * mm, v(208.11, 1.66) * mm]});
            skFitSpline(sketch, "E206", {"points": [v(208.11, 1.66) * mm, v(208.28, 5.78) * mm, v(208.5, 6.88) * mm, v(209.4, 8) * mm]});
            skFitSpline(sketch, "E207", {"points": [v(209.4, 8) * mm, v(210.88, 9.87) * mm, v(214.74, 10.52) * mm, v(216.32, 9.16) * mm]});
            skLineSegment(sketch, "E208", {"start": v(216.32, 9.16) * mm, "end": v(217.11, 8.49) * mm});
            skLineSegment(sketch, "E209", {"start": v(217.11, 8.49) * mm, "end": v(217.09, 1.32) * mm});
            skFitSpline(sketch, "E210", {"points": [v(217.09, 1.32) * mm, v(217.09, -2.6) * mm, v(216.92, -7.4) * mm, v(216.72, -9.35) * mm]});
            skFitSpline(sketch, "E211", {"points": [v(216.72, -9.35) * mm, v(215.56, -21.46) * mm, v(212.54, -38.42) * mm, v(209.35, -50.9) * mm]});
            skFitSpline(sketch, "E212", {"points": [v(209.35, -50.9) * mm, v(208.6, -53.88) * mm, v(207.89, -56.65) * mm, v(207.8, -57.05) * mm]});
            skFitSpline(sketch, "E213", {"points": [v(207.8, -57.05) * mm, v(207.66, -57.58) * mm, v(208.06, -57.3) * mm, v(209.5, -55.78) * mm]});
            skFitSpline(sketch, "E214", {"points": [v(209.5, -55.78) * mm, v(214.38, -50.61) * mm, v(219, -44.6) * mm, v(225.84, -34.6) * mm]});
            skFitSpline(sketch, "E215", {"points": [v(225.84, -34.6) * mm, v(231.68, -26) * mm, v(237.12, -18.15) * mm, v(237.94, -17.14) * mm]});
            skFitSpline(sketch, "E216", {"points": [v(237.94, -17.14) * mm, v(238.96, -15.9) * mm, v(239.3, -16.38) * mm, v(238.82, -18.4) * mm]});
            skFitSpline(sketch, "E217", {"points": [v(238.82, -18.4) * mm, v(238.22, -20.95) * mm, v(233.62, -34.78) * mm, v(230.75, -42.6) * mm]});
            skFitSpline(sketch, "E218", {"points": [v(230.75, -42.6) * mm, v(218.84, -75.22) * mm, v(205.26, -103.58) * mm, v(194.34, -118.77) * mm]});
            skFitSpline(sketch, "E219", {"points": [v(194.34, -118.77) * mm, v(186.97, -129.01) * mm, v(172.04, -144.53) * mm, v(161.23, -153.17) * mm]});
            skFitSpline(sketch, "E220", {"points": [v(161.23, -153.17) * mm, v(150.9, -161.47) * mm, v(132.48, -174.53) * mm, v(126.38, -177.9) * mm]});
            skFitSpline(sketch, "E221", {"points": [v(126.38, -177.9) * mm, v(116.59, -183.34) * mm, v(103.86, -189.86) * mm, v(101.46, -190.7) * mm]});
            skFitSpline(sketch, "E222", {"points": [v(101.46, -190.7) * mm, v(99.8, -191.3) * mm, v(97.8, -191.21) * mm, v(97.17, -190.54) * mm]});
            skFitSpline(sketch, "E223", {"points": [v(155.3, 153.32) * mm, v(154.83, 153.52) * mm, v(152.88, 155.38) * mm, v(150.93, 157.44) * mm]});
            skFitSpline(sketch, "E224", {"points": [v(150.93, 157.44) * mm, v(142.47, 166.45) * mm, v(132.28, 174.94) * mm, v(117.2, 185.5) * mm]});
            skFitSpline(sketch, "E225", {"points": [v(117.2, 185.5) * mm, v(111.03, 189.87) * mm, v(103.83, 193.57) * mm, v(84.33, 202.51) * mm]});
            skFitSpline(sketch, "E226", {"points": [v(84.33, 202.51) * mm, v(71.15, 208.55) * mm, v(65.79, 210.7) * mm, v(58.62, 212.73) * mm]});
            skFitSpline(sketch, "E227", {"points": [v(58.62, 212.73) * mm, v(34.46, 219.56) * mm, v(17.56, 221.8) * mm, v(-6.91, 221.42) * mm]});
            skFitSpline(sketch, "E228", {"points": [v(-6.91, 221.42) * mm, v(-20.04, 221.23) * mm, v(-26.95, 220.6) * mm, v(-39.43, 218.52) * mm]});
            skFitSpline(sketch, "E229", {"points": [v(-39.43, 218.52) * mm, v(-74.79, 212.62) * mm, v(-108.57, 197.46) * mm, v(-136.93, 174.8) * mm]});
            skFitSpline(sketch, "E230", {"points": [v(-136.93, 174.8) * mm, v(-142.92, 170.03) * mm, v(-146.5, 166.84) * mm, v(-153.25, 160.32) * mm]});
            skFitSpline(sketch, "E231", {"points": [v(-153.25, 160.32) * mm, v(-156.27, 157.42) * mm, v(-158.97, 154.9) * mm, v(-159.31, 154.7) * mm]});
            skFitSpline(sketch, "E232", {"points": [v(-159.31, 154.7) * mm, v(-161, 153.77) * mm, v(-162.95, 154.76) * mm, v(-164.65, 157.42) * mm]});
            skFitSpline(sketch, "E233", {"points": [v(-164.65, 157.42) * mm, v(-165.7, 159.08) * mm, v(-165.66, 160.15) * mm, v(-164.53, 161.7) * mm]});
            skFitSpline(sketch, "E234", {"points": [v(-164.53, 161.7) * mm, v(-163.12, 163.68) * mm, v(-153.53, 173.14) * mm, v(-149.35, 176.7) * mm]});
            skFitSpline(sketch, "E235", {"points": [v(-149.35, 176.7) * mm, v(-132.76, 190.8) * mm, v(-120, 199.52) * mm, v(-104.05, 207.7) * mm]});
            skFitSpline(sketch, "E236", {"points": [v(-104.05, 207.7) * mm, v(-78.23, 220.94) * mm, v(-48.48, 229.24) * mm, v(-19.1, 231.39) * mm]});
            skFitSpline(sketch, "E237", {"points": [v(-19.1, 231.39) * mm, v(-12.08, 231.9) * mm, v(1.38, 232.04) * mm, v(8.7, 231.7) * mm]});
            skFitSpline(sketch, "E238", {"points": [v(8.7, 231.7) * mm, v(31.21, 230.6) * mm, v(49.14, 227.24) * mm, v(68.3, 220.55) * mm]});
            skFitSpline(sketch, "E239", {"points": [v(68.3, 220.55) * mm, v(81.6, 215.9) * mm, v(87.24, 213.58) * mm, v(96.78, 208.8) * mm]});
            skFitSpline(sketch, "E240", {"points": [v(96.78, 208.8) * mm, v(114.44, 199.95) * mm, v(130.59, 189.05) * mm, v(144.92, 176.27) * mm]});
            skFitSpline(sketch, "E241", {"points": [v(144.92, 176.27) * mm, v(150.7, 171.1) * mm, v(159.63, 162.3) * mm, v(160.59, 160.86) * mm]});
            skFitSpline(sketch, "E242", {"points": [v(160.59, 160.86) * mm, v(161.88, 158.8) * mm, v(161.66, 156.96) * mm, v(159.8, 154.9) * mm]});
            skFitSpline(sketch, "E243", {"points": [v(159.8, 154.9) * mm, v(158.07, 153.01) * mm, v(156.94, 152.62) * mm, v(155.3, 153.32) * mm]});
            skFitSpline(sketch, "E244", {"points": [v(-23.45, -241.76) * mm, v(-25.9, -241.05) * mm, v(-28.56, -239.42) * mm, v(-32.43, -236.17) * mm]});
            skFitSpline(sketch, "E245", {"points": [v(-32.43, -236.17) * mm, v(-37.87, -231.57) * mm, v(-46.73, -224.97) * mm, v(-49.56, -223.39) * mm]});
            skFitSpline(sketch, "E246", {"points": [v(-49.56, -223.39) * mm, v(-51.48, -222.34) * mm, v(-52.4, -221.58) * mm, v(-53.5, -220.28) * mm]});
            skFitSpline(sketch, "E247", {"points": [v(-53.5, -220.28) * mm, v(-55.2, -218.22) * mm, v(-56.39, -217.49) * mm, v(-58.36, -217.2) * mm]});
            skFitSpline(sketch, "E248", {"points": [v(-58.36, -217.2) * mm, v(-60.23, -216.98) * mm, v(-61.8, -216.05) * mm, v(-62.8, -214.6) * mm]});
            skFitSpline(sketch, "E249", {"points": [v(-62.8, -214.6) * mm, v(-63.53, -213.6) * mm, v(-63.67, -213.06) * mm, v(-64, -209.84) * mm]});
            skFitSpline(sketch, "E250", {"points": [v(-64, -209.84) * mm, v(-64.46, -205.47) * mm, v(-65.2, -202.84) * mm, v(-67.73, -196.4) * mm]});
            skFitSpline(sketch, "E251", {"points": [v(-67.73, -196.4) * mm, v(-68.8, -193.73) * mm, v(-69.96, -190.65) * mm, v(-70.3, -189.55) * mm]});
            skFitSpline(sketch, "E252", {"points": [v(-70.3, -189.55) * mm, v(-71.32, -186.22) * mm, v(-71.46, -186.13) * mm, v(-77.27, -185.57) * mm]});
            skFitSpline(sketch, "E253", {"points": [v(-77.27, -185.57) * mm, v(-82.01, -185.12) * mm, v(-82.89, -184.84) * mm, v(-83.99, -183.4) * mm]});
            skFitSpline(sketch, "E254", {"points": [v(-83.99, -183.4) * mm, v(-84.78, -182.35) * mm, v(-85.85, -180) * mm, v(-85.85, -179.28) * mm]});
            skFitSpline(sketch, "E255", {"points": [v(-85.85, -179.28) * mm, v(-85.85, -178.46) * mm, v(-84.98, -177.92) * mm, v(-83.37, -177.7) * mm]});
            skFitSpline(sketch, "E256", {"points": [v(-83.37, -177.7) * mm, v(-81.25, -177.41) * mm, v(-81.05, -176.88) * mm, v(-81.87, -173.83) * mm]});
            skFitSpline(sketch, "E257", {"points": [v(-81.87, -173.83) * mm, v(-82.52, -171.26) * mm, v(-82.63, -169.09) * mm, v(-82.15, -168.6) * mm]});
            skFitSpline(sketch, "E258", {"points": [v(-82.15, -168.6) * mm, v(-81.9, -168.35) * mm, v(-81.59, -168.44) * mm, v(-80.94, -168.95) * mm]});
            skFitSpline(sketch, "E259", {"points": [v(-80.94, -168.95) * mm, v(-80.43, -169.31) * mm, v(-79.3, -169.96) * mm, v(-78.4, -170.39) * mm]});
            skFitSpline(sketch, "E260", {"points": [v(-78.4, -170.39) * mm, v(-76.99, -171.03) * mm, v(-76.48, -171.12) * mm, v(-74.87, -171) * mm]});
            skFitSpline(sketch, "E261", {"points": [v(-74.87, -171) * mm, v(-72.5, -170.84) * mm, v(-71.26, -170.19) * mm, v(-68.58, -167.76) * mm]});
            skFitSpline(sketch, "E262", {"points": [v(-68.58, -167.76) * mm, v(-66.83, -166.15) * mm, v(-65.87, -165.56) * mm, v(-62.96, -164.26) * mm]});
            skLineSegment(sketch, "E263", {"start": v(-62.96, -164.26) * mm, "end": v(-59.46, -162.68) * mm});
            skLineSegment(sketch, "E264", {"start": v(-59.46, -162.68) * mm, "end": v(-59.24, -160.54) * mm});
            skFitSpline(sketch, "E265", {"points": [v(-59.24, -160.54) * mm, v(-58.76, -155.51) * mm, v(-56.42, -152.13) * mm, v(-49.33, -146) * mm]});
            skFitSpline(sketch, "E266", {"points": [v(-49.33, -146) * mm, v(-48.57, -145.35) * mm, v(-48, -144.76) * mm, v(-48.09, -144.68) * mm]});
            skFitSpline(sketch, "E267", {"points": [v(-48.09, -144.68) * mm, v(-48.15, -144.62) * mm, v(-50, -144.22) * mm, v(-52.24, -143.86) * mm]});
            skFitSpline(sketch, "E268", {"points": [v(-52.24, -143.86) * mm, v(-56.67, -143.1) * mm, v(-58.9, -142.22) * mm, v(-58.9, -141.29) * mm]});
            skFitSpline(sketch, "E269", {"points": [v(-58.9, -141.29) * mm, v(-58.9, -140.95) * mm, v(-58.42, -140.44) * mm, v(-57.69, -139.93) * mm]});
            skLineSegment(sketch, "E270", {"start": v(-57.69, -139.93) * mm, "end": v(-56.47, -139.12) * mm});
            skLineSegment(sketch, "E271", {"start": v(-56.47, -139.12) * mm, "end": v(-57.2, -137.9) * mm});
            skFitSpline(sketch, "E272", {"points": [v(-57.2, -137.9) * mm, v(-58.05, -136.4) * mm, v(-58.08, -136.04) * mm, v(-57.32, -135.33) * mm]});
            skFitSpline(sketch, "E273", {"points": [v(-57.32, -135.33) * mm, v(-56.84, -134.91) * mm, v(-56.36, -134.83) * mm, v(-54.6, -134.88) * mm]});
            skFitSpline(sketch, "E274", {"points": [v(-54.6, -134.88) * mm, v(-50.38, -135) * mm, v(-47.72, -134.15) * mm, v(-45.97, -132.09) * mm]});
            skFitSpline(sketch, "E275", {"points": [v(-45.97, -132.09) * mm, v(-44.82, -130.73) * mm, v(-44.22, -129.2) * mm, v(-43.66, -126.1) * mm]});
            skFitSpline(sketch, "E276", {"points": [v(-43.66, -126.1) * mm, v(-42.98, -122.44) * mm, v(-41.51, -120.4) * mm, v(-37.76, -117.9) * mm]});
            skFitSpline(sketch, "E277", {"points": [v(-37.76, -117.9) * mm, v(-36.18, -116.85) * mm, v(-31.44, -114.3) * mm, v(-21.36, -109.06) * mm]});
            skFitSpline(sketch, "E278", {"points": [v(-21.36, -109.06) * mm, v(-10.98, -103.67) * mm, v(-7.45, -101.35) * mm, v(-6.35, -99.27) * mm]});
            skFitSpline(sketch, "E279", {"points": [v(-6.35, -99.27) * mm, v(-5.67, -98) * mm, v(-5.78, -95) * mm, v(-6.66, -91.48) * mm]});
            skFitSpline(sketch, "E280", {"points": [v(-6.66, -91.48) * mm, v(-7.05, -89.84) * mm, v(-7.4, -87.95) * mm, v(-7.4, -87.24) * mm]});
            skFitSpline(sketch, "E281", {"points": [v(-7.4, -87.24) * mm, v(-7.4, -85.4) * mm, v(-6.4, -83.63) * mm, v(-4.74, -82.45) * mm]});
            skFitSpline(sketch, "E282", {"points": [v(-4.74, -82.45) * mm, v(-1.18, -79.9) * mm, v(-0.62, -78.83) * mm, v(-1.7, -76.43) * mm]});
            skFitSpline(sketch, "E283", {"points": [v(-1.7, -76.43) * mm, v(-2.43, -74.77) * mm, v(-3.27, -74.26) * mm, v(-7.68, -72.82) * mm]});
            skFitSpline(sketch, "E284", {"points": [v(-7.68, -72.82) * mm, v(-9.62, -72.17) * mm, v(-11.32, -71.6) * mm, v(-11.43, -71.52) * mm]});
            skFitSpline(sketch, "E285", {"points": [v(-11.43, -71.52) * mm, v(-11.94, -71.21) * mm, v(-10.3, -70) * mm, v(-8.8, -69.55) * mm]});
            skFitSpline(sketch, "E286", {"points": [v(-8.8, -69.55) * mm, v(-7.96, -69.32) * mm, v(-7.11, -69.01) * mm, v(-6.97, -68.9) * mm]});
            skFitSpline(sketch, "E287", {"points": [v(-6.97, -68.9) * mm, v(-6.57, -68.56) * mm, v(-2.9, -67.2) * mm, v(-1.72, -66.95) * mm]});
            skFitSpline(sketch, "E288", {"points": [v(-1.72, -66.95) * mm, v(-1.04, -66.81) * mm, v(0.54, -66.9) * mm, v(2.82, -67.2) * mm]});
            skFitSpline(sketch, "E289", {"points": [v(2.82, -67.2) * mm, v(4.74, -67.49) * mm, v(7.85, -67.8) * mm, v(9.7, -67.88) * mm]});
            skFitSpline(sketch, "E290", {"points": [v(9.7, -67.88) * mm, v(11.54, -68) * mm, v(16.43, -68.33) * mm, v(20.52, -68.64) * mm]});
            skFitSpline(sketch, "E291", {"points": [v(20.52, -68.64) * mm, v(28.4, -69.24) * mm, v(29.66, -69.52) * mm, v(30.5, -70.9) * mm]});
            skFitSpline(sketch, "E292", {"points": [v(30.5, -70.9) * mm, v(30.68, -71.21) * mm, v(31.92, -72.23) * mm, v(33.2, -73.19) * mm]});
            skFitSpline(sketch, "E293", {"points": [v(33.2, -73.19) * mm, v(39.54, -77.82) * mm, v(45.64, -85.04) * mm, v(48.94, -91.96) * mm]});
            skFitSpline(sketch, "E294", {"points": [v(48.94, -91.96) * mm, v(51.96, -98.25) * mm, v(54.53, -108.89) * mm, v(54.05, -113.26) * mm]});
            skFitSpline(sketch, "E295", {"points": [v(54.05, -113.26) * mm, v(53.45, -119.1) * mm, v(48.83, -124.1) * mm, v(34.8, -134.15) * mm]});
            skFitSpline(sketch, "E296", {"points": [v(34.8, -134.15) * mm, v(29.6, -137.87) * mm, v(28.82, -138.33) * mm, v(27.55, -138.33) * mm]});
            skFitSpline(sketch, "E297", {"points": [v(27.55, -138.33) * mm, v(26.59, -138.33) * mm, v(24.41, -137.48) * mm, v(24.13, -137) * mm]});
            skFitSpline(sketch, "E298", {"points": [v(24.13, -137) * mm, v(24.02, -136.83) * mm, v(24.8, -136.12) * mm, v(25.85, -135.42) * mm]});
            skFitSpline(sketch, "E299", {"points": [v(25.85, -135.42) * mm, v(28.62, -133.53) * mm, v(30.9, -131.38) * mm, v(33.75, -127.94) * mm]});
            skFitSpline(sketch, "E300", {"points": [v(33.75, -127.94) * mm, v(38.16, -122.66) * mm, v(38.44, -122.01) * mm, v(36.92, -120.49) * mm]});
            skFitSpline(sketch, "E301", {"points": [v(36.92, -120.49) * mm, v(36.13, -119.73) * mm, v(35.9, -119.64) * mm, v(34.8, -119.75) * mm]});
            skFitSpline(sketch, "E302", {"points": [v(34.8, -119.75) * mm, v(32.9, -119.98) * mm, v(31.05, -121.36) * mm, v(25.9, -126.33) * mm]});
            skFitSpline(sketch, "E303", {"points": [v(25.9, -126.33) * mm, v(22.3, -129.83) * mm, v(20.77, -131.1) * mm, v(19.14, -132) * mm]});
            skFitSpline(sketch, "E304", {"points": [v(19.14, -132) * mm, v(12.48, -135.62) * mm, v(9.74, -137.37) * mm, v(8.95, -138.5) * mm]});
            skFitSpline(sketch, "E305", {"points": [v(8.95, -138.5) * mm, v(8.1, -139.74) * mm, v(7.6, -141.49) * mm, v(7.56, -143.15) * mm]});
            skFitSpline(sketch, "E306", {"points": [v(7.56, -143.15) * mm, v(7.56, -146.11) * mm, v(5.73, -148.82) * mm, v(3.16, -149.76) * mm]});
            skFitSpline(sketch, "E307", {"points": [v(3.16, -149.76) * mm, v(1.16, -150.49) * mm, v(0.73, -151) * mm, v(0.57, -152.83) * mm]});
            skFitSpline(sketch, "E308", {"points": [v(0.57, -152.83) * mm, v(0.45, -154.38) * mm, v(0.85, -157.4) * mm, v(1.41, -159.18) * mm]});
            skLineSegment(sketch, "E309", {"start": v(1.41, -159.18) * mm, "end": v(1.7, -160.11) * mm});
            skLineSegment(sketch, "E310", {"start": v(1.7, -160.11) * mm, "end": v(4.3, -159.92) * mm});
            skFitSpline(sketch, "E311", {"points": [v(4.3, -159.92) * mm, v(8.13, -159.63) * mm, v(8.33, -160.14) * mm, v(6.15, -164.85) * mm]});
            skFitSpline(sketch, "E312", {"points": [v(6.15, -164.85) * mm, v(5.53, -166.2) * mm, v(5.02, -167.62) * mm, v(5.02, -168.04) * mm]});
            skFitSpline(sketch, "E313", {"points": [v(5.02, -168.04) * mm, v(5.02, -168.89) * mm, v(6.04, -169.8) * mm, v(7.28, -170.08) * mm]});
            skFitSpline(sketch, "E314", {"points": [v(7.28, -170.08) * mm, v(8.41, -170.33) * mm, v(8.67, -170.72) * mm, v(9.12, -173.15) * mm]});
            skFitSpline(sketch, "E315", {"points": [v(9.12, -173.15) * mm, v(9.6, -175.63) * mm, v(9.85, -176.23) * mm, v(10.73, -176.82) * mm]});
            skFitSpline(sketch, "E316", {"points": [v(10.73, -176.82) * mm, v(11.46, -177.36) * mm, v(13.66, -177.41) * mm, v(14.82, -176.96) * mm]});
            skFitSpline(sketch, "E317", {"points": [v(14.82, -176.96) * mm, v(17.19, -176) * mm, v(19.25, -176.2) * mm, v(20.26, -177.47) * mm]});
            skFitSpline(sketch, "E318", {"points": [v(20.26, -177.47) * mm, v(21.17, -178.63) * mm, v(20.97, -179.22) * mm, v(19.02, -181.11) * mm]});
            skFitSpline(sketch, "E319", {"points": [v(19.02, -181.11) * mm, v(15.86, -184.21) * mm, v(12.42, -185.46) * mm, v(7.11, -185.46) * mm]});
            skFitSpline(sketch, "E320", {"points": [v(7.11, -185.46) * mm, v(2.34, -185.46) * mm, v(-1.64, -184.52) * mm, v(-5.81, -182.44) * mm]});
            skFitSpline(sketch, "E321", {"points": [v(-5.81, -182.44) * mm, v(-9.96, -180.38) * mm, v(-13.91, -176.82) * mm, v(-15.38, -173.89) * mm]});
            skFitSpline(sketch, "E322", {"points": [v(-15.38, -173.89) * mm, v(-15.75, -173.15) * mm, v(-16.31, -172.1) * mm, v(-16.62, -171.6) * mm]});
            skFitSpline(sketch, "E323", {"points": [v(-16.62, -171.6) * mm, v(-16.96, -171.06) * mm, v(-17.41, -169.9) * mm, v(-17.67, -169.03) * mm]});
            skFitSpline(sketch, "E324", {"points": [v(-17.67, -169.03) * mm, v(-18.03, -167.73) * mm, v(-18.26, -167.37) * mm, v(-18.82, -167.22) * mm]});
            skFitSpline(sketch, "E325", {"points": [v(-18.82, -167.22) * mm, v(-20.43, -166.83) * mm, v(-22.58, -168.21) * mm, v(-23.62, -170.3) * mm]});
            skFitSpline(sketch, "E326", {"points": [v(-23.62, -170.3) * mm, v(-24.21, -171.54) * mm, v(-24.38, -172.45) * mm, v(-24.6, -175.6) * mm]});
            skFitSpline(sketch, "E327", {"points": [v(-24.6, -175.6) * mm, v(-24.75, -177.67) * mm, v(-25.14, -181.17) * mm, v(-25.43, -183.37) * mm]});
            skFitSpline(sketch, "E328", {"points": [v(-25.43, -183.37) * mm, v(-26.56, -191.44) * mm, v(-26.5, -194.06) * mm, v(-25.06, -197.14) * mm]});
            skFitSpline(sketch, "E329", {"points": [v(-25.06, -197.14) * mm, v(-24.07, -199.31) * mm, v(-22.35, -200.78) * mm, v(-18.96, -202.45) * mm]});
            skFitSpline(sketch, "E330", {"points": [v(-18.96, -202.45) * mm, v(-16.68, -203.55) * mm, v(-15.52, -204.34) * mm, v(-13.91, -205.83) * mm]});
            skFitSpline(sketch, "E331", {"points": [v(-13.91, -205.83) * mm, v(-11.4, -208.23) * mm, v(-9.57, -209.16) * mm, v(-7.3, -209.16) * mm]});
            skFitSpline(sketch, "E332", {"points": [v(-7.3, -209.16) * mm, v(-5.53, -209.16) * mm, v(-4.12, -208.68) * mm, v(-2.65, -207.58) * mm]});
            skFitSpline(sketch, "E333", {"points": [v(-2.65, -207.58) * mm, v(-1.18, -206.45) * mm, v(-0.62, -205.32) * mm, v(-0.62, -203.5) * mm]});
            skFitSpline(sketch, "E334", {"points": [v(-0.62, -203.5) * mm, v(-0.62, -201.63) * mm, v(-1.07, -200.19) * mm, v(-2.26, -198.27) * mm]});
            skFitSpline(sketch, "E335", {"points": [v(-2.26, -198.27) * mm, v(-2.85, -197.34) * mm, v(-3.05, -196.8) * mm, v(-2.85, -196.58) * mm]});
            skFitSpline(sketch, "E336", {"points": [v(-2.85, -196.58) * mm, v(-2.45, -196.1) * mm, v(2.06, -195.81) * mm, v(3.9, -196.18) * mm]});
            skFitSpline(sketch, "E337", {"points": [v(3.9, -196.18) * mm, v(7.23, -196.83) * mm, v(8.98, -198.64) * mm, v(11.2, -203.72) * mm]});
            skFitSpline(sketch, "E338", {"points": [v(11.2, -203.72) * mm, v(12.76, -207.27) * mm, v(13.24, -207.7) * mm, v(15.27, -207.19) * mm]});
            skFitSpline(sketch, "E339", {"points": [v(15.27, -207.19) * mm, v(16.45, -206.88) * mm, v(16.6, -206.9) * mm, v(19.2, -208.26) * mm]});
            skFitSpline(sketch, "E340", {"points": [v(19.2, -208.26) * mm, v(20.66, -209.05) * mm, v(22.47, -209.78) * mm, v(23.2, -209.87) * mm]});
            skFitSpline(sketch, "E341", {"points": [v(23.2, -209.87) * mm, v(25.9, -210.3) * mm, v(28.25, -208.57) * mm, v(30.7, -204.37) * mm]});
            skFitSpline(sketch, "E342", {"points": [v(30.7, -204.37) * mm, v(31.38, -203.2) * mm, v(32.54, -201.32) * mm, v(33.3, -200.19) * mm]});
            skFitSpline(sketch, "E343", {"points": [v(33.3, -200.19) * mm, v(35.42, -196.94) * mm, v(35.14, -195.93) * mm, v(31.58, -193.56) * mm]});
            skFitSpline(sketch, "E344", {"points": [v(31.58, -193.56) * mm, v(30.06, -192.57) * mm, v(29.38, -191.13) * mm, v(29.92, -190.06) * mm]});
            skFitSpline(sketch, "E345", {"points": [v(29.92, -190.06) * mm, v(30.11, -189.66) * mm, v(30.62, -189.07) * mm, v(31.05, -188.76) * mm]});
            skLineSegment(sketch, "E346", {"start": v(31.05, -188.76) * mm, "end": v(31.8, -188.2) * mm});
            skLineSegment(sketch, "E347", {"start": v(31.8, -188.2) * mm, "end": v(33.95, -188.98) * mm});
            skFitSpline(sketch, "E348", {"points": [v(33.95, -188.98) * mm, v(35.1, -189.4) * mm, v(36.27, -189.66) * mm, v(36.52, -189.58) * mm]});
            skFitSpline(sketch, "E349", {"points": [v(36.52, -189.58) * mm, v(36.75, -189.5) * mm, v(37.2, -188.87) * mm, v(37.48, -188.22) * mm]});
            skFitSpline(sketch, "E350", {"points": [v(37.48, -188.22) * mm, v(37.76, -187.54) * mm, v(38.41, -186.64) * mm, v(38.86, -186.2) * mm]});
            skFitSpline(sketch, "E351", {"points": [v(38.86, -186.2) * mm, v(39.34, -185.71) * mm, v(39.74, -185.2) * mm, v(39.74, -185) * mm]});
            skFitSpline(sketch, "E352", {"points": [v(39.74, -185) * mm, v(39.74, -184.84) * mm, v(40.39, -183.4) * mm, v(41.15, -181.79) * mm]});
            skFitSpline(sketch, "E353", {"points": [v(41.15, -181.79) * mm, v(42.36, -179.36) * mm, v(42.64, -178.97) * mm, v(42.98, -179.25) * mm]});
            skFitSpline(sketch, "E354", {"points": [v(42.98, -179.25) * mm, v(43.2, -179.44) * mm, v(43.4, -179.92) * mm, v(43.4, -180.35) * mm]});
            skFitSpline(sketch, "E355", {"points": [v(43.4, -180.35) * mm, v(43.4, -180.77) * mm, v(43.58, -181.34) * mm, v(43.8, -181.65) * mm]});
            skFitSpline(sketch, "E356", {"points": [v(43.8, -181.65) * mm, v(44, -181.96) * mm, v(44.3, -182.97) * mm, v(44.48, -183.9) * mm]});
            skFitSpline(sketch, "E357", {"points": [v(44.48, -183.9) * mm, v(44.7, -185.34) * mm, v(44.68, -185.94) * mm, v(44.2, -187.71) * mm]});
            skFitSpline(sketch, "E358", {"points": [v(44.2, -187.71) * mm, v(43.69, -189.52) * mm, v(43.58, -191.13) * mm, v(43.4, -199) * mm]});
            skFitSpline(sketch, "E359", {"points": [v(43.4, -199) * mm, v(43.18, -208.88) * mm, v(43.01, -210.04) * mm, v(41.52, -213.06) * mm]});
            skFitSpline(sketch, "E360", {"points": [v(41.52, -213.06) * mm, v(40.58, -214.92) * mm, v(37.62, -217.74) * mm, v(35.36, -218.96) * mm]});
            skFitSpline(sketch, "E361", {"points": [v(35.36, -218.96) * mm, v(34.43, -219.44) * mm, v(32.03, -220.48) * mm, v(30, -221.3) * mm]});
            skFitSpline(sketch, "E362", {"points": [v(30, -221.3) * mm, v(28, -222.09) * mm, v(25.26, -223.36) * mm, v(23.93, -224.12) * mm]});
            skFitSpline(sketch, "E363", {"points": [v(23.93, -224.12) * mm, v(14.82, -229.29) * mm, v(8.02, -231.23) * mm, v(-1.18, -231.23) * mm]});
            skFitSpline(sketch, "E364", {"points": [v(-1.18, -231.23) * mm, v(-8.27, -231.26) * mm, v(-16.57, -229.82) * mm, v(-21, -227.82) * mm]});
            skFitSpline(sketch, "E365", {"points": [v(-21, -227.82) * mm, v(-23.5, -226.66) * mm, v(-24.72, -226.66) * mm, v(-25.31, -227.79) * mm]});
            skFitSpline(sketch, "E366", {"points": [v(-25.31, -227.79) * mm, v(-26.22, -229.51) * mm, v(-25.68, -231.1) * mm, v(-23.34, -233.8) * mm]});
            skFitSpline(sketch, "E367", {"points": [v(-23.34, -233.8) * mm, v(-21.7, -235.72) * mm, v(-20.46, -236.26) * mm, v(-17.58, -236.37) * mm]});
            skFitSpline(sketch, "E368", {"points": [v(-17.58, -236.37) * mm, v(-15.92, -236.43) * mm, v(-15.44, -236.54) * mm, v(-15.13, -236.96) * mm]});
            skFitSpline(sketch, "E369", {"points": [v(-15.13, -236.96) * mm, v(-14.17, -238.29) * mm, v(-15.18, -239.98) * mm, v(-17.67, -241.2) * mm]});
            skFitSpline(sketch, "E370", {"points": [v(-17.67, -241.2) * mm, v(-19.53, -242.1) * mm, v(-21.5, -242.3) * mm, v(-23.45, -241.76) * mm]});
            skFitSpline(sketch, "E371", {"points": [v(-23.25, -93.85) * mm, v(-23.37, -93.76) * mm, v(-22.75, -92.27) * mm, v(-21.93, -90.54) * mm]});
            skFitSpline(sketch, "E372", {"points": [v(-21.93, -90.54) * mm, v(-19.78, -86.09) * mm, v(-19.2, -83.69) * mm, v(-19.33, -80.24) * mm]});
            skFitSpline(sketch, "E373", {"points": [v(-19.33, -80.24) * mm, v(-19.39, -78.75) * mm, v(-19.61, -76.77) * mm, v(-19.81, -75.84) * mm]});
            skFitSpline(sketch, "E374", {"points": [v(-19.81, -75.84) * mm, v(-20.2, -74.2) * mm, v(-20.2, -74.2) * mm, v(-19.53, -73.64) * mm]});
            skFitSpline(sketch, "E375", {"points": [v(-19.53, -73.64) * mm, v(-18.9, -73.16) * mm, v(-18.57, -73.1) * mm, v(-17.02, -73.24) * mm]});
            skFitSpline(sketch, "E376", {"points": [v(-17.02, -73.24) * mm, v(-16.03, -73.36) * mm, v(-14.87, -73.61) * mm, v(-14.45, -73.84) * mm]});
            skFitSpline(sketch, "E377", {"points": [v(-14.45, -73.84) * mm, v(-13.3, -74.43) * mm, v(-11.71, -76.4) * mm, v(-10.7, -78.5) * mm]});
            skFitSpline(sketch, "E378", {"points": [v(-10.7, -78.5) * mm, v(-9.88, -80.19) * mm, v(-9.8, -80.55) * mm, v(-9.8, -83.15) * mm]});
            skFitSpline(sketch, "E379", {"points": [v(-9.8, -83.15) * mm, v(-9.8, -85.7) * mm, v(-9.88, -86.09) * mm, v(-10.55, -87.27) * mm]});
            skFitSpline(sketch, "E380", {"points": [v(-10.55, -87.27) * mm, v(-12.16, -90) * mm, v(-14.76, -91.73) * mm, v(-19, -92.86) * mm]});
            skFitSpline(sketch, "E381", {"points": [v(-19, -92.86) * mm, v(-20.15, -93.17) * mm, v(-21.48, -93.56) * mm, v(-21.9, -93.73) * mm]});
            skFitSpline(sketch, "E382", {"points": [v(-21.9, -93.73) * mm, v(-22.77, -94.04) * mm, v(-23.03, -94.07) * mm, v(-23.25, -93.85) * mm]});
            skFitSpline(sketch, "E383", {"points": [v(-1.01, -63.23) * mm, v(-4.97, -62.66) * mm, v(-9.93, -60.77) * mm, v(-12.87, -58.77) * mm]});
            skFitSpline(sketch, "E384", {"points": [v(-12.87, -58.77) * mm, v(-13.57, -58.26) * mm, v(-15.21, -57.36) * mm, v(-16.48, -56.76) * mm]});
            skFitSpline(sketch, "E385", {"points": [v(-16.48, -56.76) * mm, v(-23.4, -53.49) * mm, v(-28.53, -54.14) * mm, v(-35.33, -59.13) * mm]});
            skFitSpline(sketch, "E386", {"points": [v(-35.33, -59.13) * mm, v(-37.5, -60.74) * mm, v(-39.62, -61.4) * mm, v(-41.94, -61.22) * mm]});
            skFitSpline(sketch, "E387", {"points": [v(-41.94, -61.22) * mm, v(-44.34, -61.02) * mm, v(-46.2, -60) * mm, v(-48.23, -57.78) * mm]});
            skFitSpline(sketch, "E388", {"points": [v(-48.23, -57.78) * mm, v(-49.16, -56.76) * mm, v(-50.3, -55.75) * mm, v(-50.74, -55.5) * mm]});
            skFitSpline(sketch, "E389", {"points": [v(-50.74, -55.5) * mm, v(-51.7, -55.01) * mm, v(-54.6, -54.93) * mm, v(-56.47, -55.38) * mm]});
            skFitSpline(sketch, "E390", {"points": [v(-56.47, -55.38) * mm, v(-57.15, -55.52) * mm, v(-58.08, -55.58) * mm, v(-58.53, -55.46) * mm]});
            skFitSpline(sketch, "E391", {"points": [v(-58.53, -55.46) * mm, v(-59.63, -55.24) * mm, v(-60.45, -53.86) * mm, v(-60.45, -52.33) * mm]});
            skFitSpline(sketch, "E392", {"points": [v(-60.45, -52.33) * mm, v(-60.45, -51.15) * mm, v(-60.48, -51.12) * mm, v(-61.38, -51.12) * mm]});
            skFitSpline(sketch, "E393", {"points": [v(-61.38, -51.12) * mm, v(-62.96, -51.12) * mm, v(-64.85, -51.94) * mm, v(-67, -53.55) * mm]});
            skFitSpline(sketch, "E394", {"points": [v(-67, -53.55) * mm, v(-72.59, -57.67) * mm, v(-76.74, -58.54) * mm, v(-80.94, -56.48) * mm]});
            skFitSpline(sketch, "E395", {"points": [v(-80.94, -56.48) * mm, v(-83.2, -55.38) * mm, v(-84.8, -53.91) * mm, v(-87.32, -50.75) * mm]});
            skFitSpline(sketch, "E396", {"points": [v(-87.32, -50.75) * mm, v(-91.3, -45.67) * mm, v(-93.84, -43.92) * mm, v(-98.4, -43.08) * mm]});
            skFitSpline(sketch, "E397", {"points": [v(-98.4, -43.08) * mm, v(-103.66, -42.09) * mm, v(-105.3, -40.25) * mm, v(-104.9, -35.7) * mm]});
            skFitSpline(sketch, "E398", {"points": [v(-104.9, -35.7) * mm, v(-104.56, -31.73) * mm, v(-105.5, -30.8) * mm, v(-109.98, -30.38) * mm]});
            skFitSpline(sketch, "E399", {"points": [v(-109.98, -30.38) * mm, v(-113.17, -30.06) * mm, v(-114.92, -29.05) * mm, v(-114.92, -27.47) * mm]});
            skFitSpline(sketch, "E400", {"points": [v(-114.92, -27.47) * mm, v(-114.92, -25.44) * mm, v(-111.2, -21.12) * mm, v(-108.17, -19.7) * mm]});
            skFitSpline(sketch, "E401", {"points": [v(-108.17, -19.7) * mm, v(-106.5, -18.92) * mm, v(-106.06, -18.8) * mm, v(-103.91, -18.83) * mm]});
            skFitSpline(sketch, "E402", {"points": [v(-103.91, -18.83) * mm, v(-101.97, -18.86) * mm, v(-101.1, -19.03) * mm, v(-99.17, -19.76) * mm]});
            skFitSpline(sketch, "E403", {"points": [v(-99.17, -19.76) * mm, v(-96.4, -20.8) * mm, v(-94.97, -20.86) * mm, v(-93.92, -20.05) * mm]});
            skFitSpline(sketch, "E404", {"points": [v(-93.92, -20.05) * mm, v(-92.17, -18.66) * mm, v(-91.86, -16.77) * mm, v(-93.25, -15.81) * mm]});
            skFitSpline(sketch, "E405", {"points": [v(-93.25, -15.81) * mm, v(-93.75, -15.47) * mm, v(-94.94, -14.46) * mm, v(-95.87, -13.58) * mm]});
            skFitSpline(sketch, "E406", {"points": [v(-95.87, -13.58) * mm, v(-99.34, -10.3) * mm, v(-101, -9.72) * mm, v(-104.7, -10.37) * mm]});
            skFitSpline(sketch, "E407", {"points": [v(-104.7, -10.37) * mm, v(-107.33, -10.82) * mm, v(-112.63, -10.87) * mm, v(-115.68, -10.45) * mm]});
            skFitSpline(sketch, "E408", {"points": [v(-115.68, -10.45) * mm, v(-118.25, -10.11) * mm, v(-120.6, -9.12) * mm, v(-121.92, -7.85) * mm]});
            skFitSpline(sketch, "E409", {"points": [v(-121.92, -7.85) * mm, v(-122.46, -7.35) * mm, v(-123.44, -5.8) * mm, v(-124.12, -4.35) * mm]});
            skFitSpline(sketch, "E410", {"points": [v(-124.12, -4.35) * mm, v(-125.05, -2.44) * mm, v(-125.81, -1.3) * mm, v(-127.11, 0.02) * mm]});
            skFitSpline(sketch, "E411", {"points": [v(-127.11, 0.02) * mm, v(-128.78, 1.69) * mm, v(-134.45, 6) * mm, v(-138.97, 9.08) * mm]});
            skFitSpline(sketch, "E412", {"points": [v(-138.97, 9.08) * mm, v(-143, 11.76) * mm, v(-147.4, 12.38) * mm, v(-151.95, 10.86) * mm]});
            skLineSegment(sketch, "E413", {"start": v(-151.95, 10.86) * mm, "end": v(-154.43, 10.01) * mm});
            skLineSegment(sketch, "E414", {"start": v(-154.43, 10.01) * mm, "end": v(-155.14, 10.69) * mm});
            skFitSpline(sketch, "E415", {"points": [v(-155.14, 10.69) * mm, v(-156.4, 11.9) * mm, v(-155.93, 12.75) * mm, v(-153.44, 13.74) * mm]});
            skFitSpline(sketch, "E416", {"points": [v(-153.44, 13.74) * mm, v(-152.65, 14.05) * mm, v(-150.31, 15.12) * mm, v(-148.22, 16.14) * mm]});
            skFitSpline(sketch, "E417", {"points": [v(-148.22, 16.14) * mm, v(-142.35, 18.93) * mm, v(-141.03, 19.3) * mm, v(-137.36, 19.3) * mm]});
            skFitSpline(sketch, "E418", {"points": [v(-137.36, 19.3) * mm, v(-134.48, 19.27) * mm, v(-134.05, 19.18) * mm, v(-131.57, 18.25) * mm]});
            skFitSpline(sketch, "E419", {"points": [v(-131.57, 18.25) * mm, v(-128.13, 16.95) * mm, v(-127.28, 16.78) * mm, v(-126.04, 17.18) * mm]});
            skFitSpline(sketch, "E420", {"points": [v(-126.04, 17.18) * mm, v(-124.6, 17.66) * mm, v(-123.61, 19.83) * mm, v(-123.44, 22.88) * mm]});
            skFitSpline(sketch, "E421", {"points": [v(-123.44, 22.88) * mm, v(-123.22, 26.92) * mm, v(-124.49, 28.7) * mm, v(-128.78, 30.39) * mm]});
            skFitSpline(sketch, "E422", {"points": [v(-128.78, 30.39) * mm, v(-135.97, 33.18) * mm, v(-144.24, 33.92) * mm, v(-153.16, 32.56) * mm]});
            skFitSpline(sketch, "E423", {"points": [v(-153.16, 32.56) * mm, v(-158.72, 31.71) * mm, v(-162.02, 30.47) * mm, v(-164.96, 28.07) * mm]});
            skFitSpline(sketch, "E424", {"points": [v(-164.96, 28.07) * mm, v(-167.3, 26.18) * mm, v(-168.1, 25.84) * mm, v(-170, 25.98) * mm]});
            skFitSpline(sketch, "E425", {"points": [v(-170, 25.98) * mm, v(-171.36, 26.1) * mm, v(-172.44, 26.5) * mm, v(-175.96, 28.24) * mm]});
            skFitSpline(sketch, "E426", {"points": [v(-175.96, 28.24) * mm, v(-178.34, 29.4) * mm, v(-180.68, 30.44) * mm, v(-181.21, 30.56) * mm]});
            skFitSpline(sketch, "E427", {"points": [v(-181.21, 30.56) * mm, v(-182.48, 30.78) * mm, v(-184.12, 30.33) * mm, v(-185.2, 29.43) * mm]});
            skFitSpline(sketch, "E428", {"points": [v(-185.2, 29.43) * mm, v(-186.04, 28.72) * mm, v(-186.07, 28.7) * mm, v(-186.6, 29.17) * mm]});
            skFitSpline(sketch, "E429", {"points": [v(-186.6, 29.17) * mm, v(-187.37, 29.88) * mm, v(-187.73, 31.35) * mm, v(-187.73, 33.83) * mm]});
            skFitSpline(sketch, "E430", {"points": [v(-187.73, 33.83) * mm, v(-187.73, 34.99) * mm, v(-187.9, 36.26) * mm, v(-188.1, 36.62) * mm]});
            skFitSpline(sketch, "E431", {"points": [v(-188.1, 36.62) * mm, v(-188.66, 37.75) * mm, v(-190.02, 38.35) * mm, v(-192.67, 38.66) * mm]});
            skFitSpline(sketch, "E432", {"points": [v(-192.67, 38.66) * mm, v(-197.5, 39.2) * mm, v(-199.02, 40.83) * mm, v(-199.02, 45.4) * mm]});
            skFitSpline(sketch, "E433", {"points": [v(-199.02, 45.4) * mm, v(-199.02, 47.55) * mm, v(-199.08, 47.74) * mm, v(-199.78, 48.4) * mm]});
            skFitSpline(sketch, "E434", {"points": [v(-199.78, 48.4) * mm, v(-200.24, 48.76) * mm, v(-201.3, 49.72) * mm, v(-202.21, 50.54) * mm]});
            skFitSpline(sketch, "E435", {"points": [v(-202.21, 50.54) * mm, v(-203.09, 51.33) * mm, v(-204.36, 52.82) * mm, v(-205, 53.84) * mm]});
            skFitSpline(sketch, "E436", {"points": [v(-205, 53.84) * mm, v(-205.65, 54.86) * mm, v(-206.78, 56.44) * mm, v(-207.55, 57.34) * mm]});
            skFitSpline(sketch, "E437", {"points": [v(-207.55, 57.34) * mm, v(-209.04, 59.17) * mm, v(-209.15, 59.65) * mm, v(-208.3, 60.75) * mm]});
            skFitSpline(sketch, "E438", {"points": [v(-208.3, 60.75) * mm, v(-207.57, 61.69) * mm, v(-206.47, 61.71) * mm, v(-205.2, 60.78) * mm]});
            skFitSpline(sketch, "E439", {"points": [v(-205.2, 60.78) * mm, v(-202.83, 59.03) * mm, v(-200.4, 58.13) * mm, v(-195.21, 57.11) * mm]});
            skFitSpline(sketch, "E440", {"points": [v(-195.21, 57.11) * mm, v(-190.27, 56.13) * mm, v(-190.05, 56.1) * mm, v(-187.37, 56.4) * mm]});
            skFitSpline(sketch, "E441", {"points": [v(-187.37, 56.4) * mm, v(-181.95, 57.03) * mm, v(-180.17, 58.36) * mm, v(-180.45, 61.54) * mm]});
            skFitSpline(sketch, "E442", {"points": [v(-180.45, 61.54) * mm, v(-180.62, 63.13) * mm, v(-181.3, 64.2) * mm, v(-182.62, 64.99) * mm]});
            skFitSpline(sketch, "E443", {"points": [v(-182.62, 64.99) * mm, v(-184.85, 66.29) * mm, v(-196.43, 67.08) * mm, v(-205.32, 66.51) * mm]});
            skFitSpline(sketch, "E444", {"points": [v(-205.32, 66.51) * mm, v(-208.59, 66.31) * mm, v(-214.04, 66.14) * mm, v(-217.37, 66.17) * mm]});
            skFitSpline(sketch, "E445", {"points": [v(-217.37, 66.17) * mm, v(-222.7, 66.17) * mm, v(-223.72, 66.26) * mm, v(-225.7, 66.8) * mm]});
            skFitSpline(sketch, "E446", {"points": [v(-225.7, 66.8) * mm, v(-229.39, 67.8) * mm, v(-235, 70.77) * mm, v(-234.38, 71.4) * mm]});
            skFitSpline(sketch, "E447", {"points": [v(-234.38, 71.4) * mm, v(-234.24, 71.54) * mm, v(-232.89, 71.76) * mm, v(-231.34, 71.93) * mm]});
            skFitSpline(sketch, "E448", {"points": [v(-231.34, 71.93) * mm, v(-225.58, 72.55) * mm, v(-223.86, 73.34) * mm, v(-223.86, 75.4) * mm]});
            skFitSpline(sketch, "E449", {"points": [v(-223.86, 75.4) * mm, v(-223.86, 76.36) * mm, v(-224.06, 76.7) * mm, v(-225.47, 78.11) * mm]});
            skFitSpline(sketch, "E450", {"points": [v(-225.47, 78.11) * mm, v(-226.37, 78.99) * mm, v(-228.68, 80.9) * mm, v(-230.63, 82.34) * mm]});
            skFitSpline(sketch, "E451", {"points": [v(-230.63, 82.34) * mm, v(-234.05, 84.88) * mm, v(-238.82, 89.26) * mm, v(-238.82, 89.85) * mm]});
            skFitSpline(sketch, "E452", {"points": [v(-238.82, 89.85) * mm, v(-238.82, 90.02) * mm, v(-239.04, 90.27) * mm, v(-239.32, 90.47) * mm]});
            skFitSpline(sketch, "E453", {"points": [v(-239.32, 90.47) * mm, v(-239.75, 90.73) * mm, v(-239.89, 91.3) * mm, v(-240.03, 92.98) * mm]});
            skFitSpline(sketch, "E454", {"points": [v(-240.03, 92.98) * mm, v(-240.31, 96.2) * mm, v(-239.7, 96.6) * mm, v(-236.67, 95.07) * mm]});
            skFitSpline(sketch, "E455", {"points": [v(-236.67, 95.07) * mm, v(-234.7, 94.06) * mm, v(-231.17, 93.1) * mm, v(-229.45, 93.1) * mm]});
            skFitSpline(sketch, "E456", {"points": [v(-229.45, 93.1) * mm, v(-228.12, 93.1) * mm, v(-226.62, 93.86) * mm, v(-226.12, 94.8) * mm]});
            skFitSpline(sketch, "E457", {"points": [v(-226.12, 94.8) * mm, v(-225.72, 95.52) * mm, v(-221.1, 97.87) * mm, v(-217.62, 99.05) * mm]});
            skFitSpline(sketch, "E458", {"points": [v(-217.62, 99.05) * mm, v(-214.49, 100.15) * mm, v(-213.42, 101.03) * mm, v(-213.42, 102.5) * mm]});
            skFitSpline(sketch, "E459", {"points": [v(-213.42, 102.5) * mm, v(-213.42, 104.5) * mm, v(-214.83, 105.2) * mm, v(-218.83, 105.23) * mm]});
            skFitSpline(sketch, "E460", {"points": [v(-218.83, 105.23) * mm, v(-221.23, 105.23) * mm, v(-223.55, 105.66) * mm, v(-224.85, 106.28) * mm]});
            skFitSpline(sketch, "E461", {"points": [v(-224.85, 106.28) * mm, v(-226.96, 107.35) * mm, v(-227.9, 108.93) * mm, v(-228.34, 112.1) * mm]});
            skFitSpline(sketch, "E462", {"points": [v(-228.34, 112.1) * mm, v(-228.51, 113.3) * mm, v(-228.82, 114.69) * mm, v(-229.05, 115.2) * mm]});
            skFitSpline(sketch, "E463", {"points": [v(-229.05, 115.2) * mm, v(-229.61, 116.55) * mm, v(-231.08, 118.13) * mm, v(-232.58, 118.98) * mm]});
            skFitSpline(sketch, "E464", {"points": [v(-232.58, 118.98) * mm, v(-236.73, 121.38) * mm, v(-237.97, 122.9) * mm, v(-237.97, 125.64) * mm]});
            skFitSpline(sketch, "E465", {"points": [v(-237.97, 125.64) * mm, v(-237.97, 127.67) * mm, v(-237.15, 129.48) * mm, v(-234.95, 132.21) * mm]});
            skFitSpline(sketch, "E466", {"points": [v(-234.95, 132.21) * mm, v(-232.8, 134.87) * mm, v(-231.76, 136.56) * mm, v(-231.76, 137.32) * mm]});
            skFitSpline(sketch, "E467", {"points": [v(-231.76, 137.32) * mm, v(-231.76, 138.2) * mm, v(-232.95, 139.44) * mm, v(-235.15, 140.88) * mm]});
            skFitSpline(sketch, "E468", {"points": [v(-235.15, 140.88) * mm, v(-236.92, 142.03) * mm, v(-237.46, 142.82) * mm, v(-236.9, 143.39) * mm]});
            skFitSpline(sketch, "E469", {"points": [v(-236.9, 143.39) * mm, v(-236.76, 143.53) * mm, v(-235.29, 143.78) * mm, v(-233.65, 143.9) * mm]});
            skFitSpline(sketch, "E470", {"points": [v(-233.65, 143.9) * mm, v(-231.99, 144.04) * mm, v(-230.4, 144.3) * mm, v(-230.07, 144.46) * mm]});
            skFitSpline(sketch, "E471", {"points": [v(-230.07, 144.46) * mm, v(-229.16, 144.94) * mm, v(-228.37, 146.44) * mm, v(-228.37, 147.65) * mm]});
            skFitSpline(sketch, "E472", {"points": [v(-228.37, 147.65) * mm, v(-228.37, 149.46) * mm, v(-228.97, 150.16) * mm, v(-231.68, 151.6) * mm]});
            skFitSpline(sketch, "E473", {"points": [v(-231.68, 151.6) * mm, v(-233.03, 152.34) * mm, v(-235.43, 153.75) * mm, v(-236.98, 154.73) * mm]});
            skLineSegment(sketch, "E474", {"start": v(-236.98, 154.73) * mm, "end": v(-239.8, 156.51) * mm});
            skLineSegment(sketch, "E475", {"start": v(-239.8, 156.51) * mm, "end": v(-240.6, 158.88) * mm});
            skFitSpline(sketch, "E476", {"points": [v(-240.6, 158.88) * mm, v(-242.74, 165.35) * mm, v(-242.82, 166.05) * mm, v(-242.88, 175.79) * mm]});
            skFitSpline(sketch, "E477", {"points": [v(-242.88, 175.79) * mm, v(-242.94, 184.62) * mm, v(-243.13, 186.85) * mm, v(-244.1, 190.6) * mm]});
            skFitSpline(sketch, "E478", {"points": [v(-244.1, 190.6) * mm, v(-244.35, 191.54) * mm, v(-244.54, 193.57) * mm, v(-244.54, 195.12) * mm]});
            skFitSpline(sketch, "E479", {"points": [v(-244.54, 195.12) * mm, v(-244.57, 197.63) * mm, v(-244.49, 198.08) * mm, v(-243.92, 199.02) * mm]});
            skFitSpline(sketch, "E480", {"points": [v(-243.92, 199.02) * mm, v(-243.13, 200.31) * mm, v(-241.38, 201.56) * mm, v(-240.93, 201.19) * mm]});
            skFitSpline(sketch, "E481", {"points": [v(-240.93, 201.19) * mm, v(-240.73, 201.05) * mm, v(-240.42, 200.17) * mm, v(-240.23, 199.3) * mm]});
            skFitSpline(sketch, "E482", {"points": [v(-240.23, 199.3) * mm, v(-239.66, 196.73) * mm, v(-238.05, 192.27) * mm, v(-236.56, 189.17) * mm]});
            skFitSpline(sketch, "E483", {"points": [v(-236.56, 189.17) * mm, v(-234.78, 185.47) * mm, v(-233.57, 184.48) * mm, v(-232.15, 185.5) * mm]});
            skFitSpline(sketch, "E484", {"points": [v(-232.15, 185.5) * mm, v(-231.65, 185.9) * mm, v(-231.62, 186.23) * mm, v(-231.7, 190.75) * mm]});
            skFitSpline(sketch, "E485", {"points": [v(-231.7, 190.75) * mm, v(-231.76, 194.19) * mm, v(-231.7, 195.68) * mm, v(-231.45, 196) * mm]});
            skFitSpline(sketch, "E486", {"points": [v(-231.45, 196) * mm, v(-230.88, 196.67) * mm, v(-229.78, 196.45) * mm, v(-228.37, 195.37) * mm]});
            skFitSpline(sketch, "E487", {"points": [v(-228.37, 195.37) * mm, v(-227.13, 194.41) * mm, v(-226.96, 194.16) * mm, v(-226.12, 191.48) * mm]});
            skFitSpline(sketch, "E488", {"points": [v(-226.12, 191.48) * mm, v(-224.42, 186.29) * mm, v(-218.98, 176.32) * mm, v(-214.18, 169.58) * mm]});
            skFitSpline(sketch, "E489", {"points": [v(-214.18, 169.58) * mm, v(-211.16, 165.35) * mm, v(-206.9, 160.44) * mm, v(-207.32, 161.68) * mm]});
            skFitSpline(sketch, "E490", {"points": [v(-207.32, 161.68) * mm, v(-207.4, 161.9) * mm, v(-207.91, 163.7) * mm, v(-208.48, 165.71) * mm]});
            skFitSpline(sketch, "E491", {"points": [v(-208.48, 165.71) * mm, v(-210.7, 173.59) * mm, v(-213.05, 178.67) * mm, v(-215.84, 181.74) * mm]});
            skFitSpline(sketch, "E492", {"points": [v(-215.84, 181.74) * mm, v(-217.76, 183.83) * mm, v(-218.92, 185.86) * mm, v(-220.95, 190.83) * mm]});
            skFitSpline(sketch, "E493", {"points": [v(-220.95, 190.83) * mm, v(-223.5, 197.07) * mm, v(-224, 197.8) * mm, v(-229.02, 202.57) * mm]});
            skFitSpline(sketch, "E494", {"points": [v(-229.02, 202.57) * mm, v(-230.52, 203.95) * mm, v(-231.48, 206.13) * mm, v(-231.48, 208.05) * mm]});
            skFitSpline(sketch, "E495", {"points": [v(-231.48, 208.05) * mm, v(-231.48, 208.7) * mm, v(-231.11, 210.2) * mm, v(-230.66, 211.35) * mm]});
            skFitSpline(sketch, "E496", {"points": [v(-230.66, 211.35) * mm, v(-229.45, 214.45) * mm, v(-229.3, 215.98) * mm, v(-230.04, 218.32) * mm]});
            skFitSpline(sketch, "E497", {"points": [v(-230.04, 218.32) * mm, v(-230.94, 221.31) * mm, v(-233.93, 224.92) * mm, v(-237.49, 227.35) * mm]});
            skFitSpline(sketch, "E498", {"points": [v(-237.49, 227.35) * mm, v(-238.25, 227.89) * mm, v(-238.87, 228.56) * mm, v(-238.98, 228.99) * mm]});
            skFitSpline(sketch, "E499", {"points": [v(-238.98, 228.99) * mm, v(-239.38, 230.6) * mm, v(-237.18, 232.23) * mm, v(-235.4, 231.61) * mm]});
            skFitSpline(sketch, "E500", {"points": [v(-235.4, 231.61) * mm, v(-233.48, 230.93) * mm, v(-228.2, 227.94) * mm, v(-227.19, 226.96) * mm]});
            skFitSpline(sketch, "E501", {"points": [v(-227.19, 226.96) * mm, v(-226.2, 225.97) * mm, v(-225.52, 224.64) * mm, v(-225.16, 222.86) * mm]});
            skFitSpline(sketch, "E502", {"points": [v(-225.16, 222.86) * mm, v(-224.87, 221.54) * mm, v(-223.2, 221.5) * mm, v(-222.7, 222.8) * mm]});
            skFitSpline(sketch, "E503", {"points": [v(-222.7, 222.8) * mm, v(-222.56, 223.2) * mm, v(-222.53, 225.04) * mm, v(-222.64, 226.96) * mm]});
            skFitSpline(sketch, "E504", {"points": [v(-222.64, 226.96) * mm, v(-222.79, 229.92) * mm, v(-222.73, 230.74) * mm, v(-222.2, 232.8) * mm]});
            skFitSpline(sketch, "E505", {"points": [v(-222.2, 232.8) * mm, v(-221.6, 235.22) * mm, v(-219.93, 239) * mm, v(-218.7, 240.81) * mm]});
            skFitSpline(sketch, "E506", {"points": [v(-218.7, 240.81) * mm, v(-218.02, 241.83) * mm, v(-214.32, 245.16) * mm, v(-213.22, 245.75) * mm]});
            skFitSpline(sketch, "E507", {"points": [v(-213.22, 245.75) * mm, v(-211.78, 246.51) * mm, v(-210.31, 245.78) * mm, v(-210.31, 244.31) * mm]});
            skFitSpline(sketch, "E508", {"points": [v(-210.31, 244.31) * mm, v(-210.31, 243.92) * mm, v(-210.62, 243.04) * mm, v(-210.99, 242.36) * mm]});
            skFitSpline(sketch, "E509", {"points": [v(-210.99, 242.36) * mm, v(-211.75, 241) * mm, v(-213.13, 235.28) * mm, v(-213.13, 233.56) * mm]});
            skFitSpline(sketch, "E510", {"points": [v(-213.13, 233.56) * mm, v(-213.13, 231.98) * mm, v(-212.46, 230.77) * mm, v(-210.82, 229.38) * mm]});
            skFitSpline(sketch, "E511", {"points": [v(-210.82, 229.38) * mm, v(-208.25, 227.2) * mm, v(-207.77, 224.9) * mm, v(-209.1, 221.03) * mm]});
            skFitSpline(sketch, "E512", {"points": [v(-209.1, 221.03) * mm, v(-210.06, 218.2) * mm, v(-210.09, 215.95) * mm, v(-209.18, 214.11) * mm]});
            skFitSpline(sketch, "E513", {"points": [v(-209.18, 214.11) * mm, v(-208.84, 213.38) * mm, v(-207.4, 211.55) * mm, v(-206.02, 210.02) * mm]});
            skFitSpline(sketch, "E514", {"points": [v(-206.02, 210.02) * mm, v(-204.61, 208.53) * mm, v(-203.14, 206.8) * mm, v(-202.78, 206.21) * mm]});
            skFitSpline(sketch, "E515", {"points": [v(-202.78, 206.21) * mm, v(-201.96, 204.97) * mm, v(-201.82, 204.94) * mm, v(-201.17, 205.68) * mm]});
            skFitSpline(sketch, "E516", {"points": [v(-201.17, 205.68) * mm, v(-200.57, 206.32) * mm, v(-200.3, 208.53) * mm, v(-200, 214.31) * mm]});
            skFitSpline(sketch, "E517", {"points": [v(-200, 214.31) * mm, v(-199.73, 220.94) * mm, v(-199.05, 223.17) * mm, v(-196.57, 225.49) * mm]});
            skFitSpline(sketch, "E518", {"points": [v(-196.57, 225.49) * mm, v(-195.6, 226.4) * mm, v(-194.79, 226.87) * mm, v(-193.8, 227.12) * mm]});
            skFitSpline(sketch, "E519", {"points": [v(-193.8, 227.12) * mm, v(-188.27, 228.48) * mm, v(-187.82, 228.99) * mm, v(-187.3, 234.07) * mm]});
            skFitSpline(sketch, "E520", {"points": [v(-187.3, 234.07) * mm, v(-186.94, 237.6) * mm, v(-186.24, 239.37) * mm, v(-184.4, 241.15) * mm]});
            skFitSpline(sketch, "E521", {"points": [v(-184.4, 241.15) * mm, v(-182.23, 243.27) * mm, v(-178.87, 244.93) * mm, v(-176.33, 245.13) * mm]});
            skFitSpline(sketch, "E522", {"points": [v(-176.33, 245.13) * mm, v(-174.02, 245.33) * mm, v(-173.88, 245.1) * mm, v(-174.72, 242.17) * mm]});
            skFitSpline(sketch, "E523", {"points": [v(-174.72, 242.17) * mm, v(-176, 237.65) * mm, v(-177.1, 235.45) * mm, v(-179.66, 232.46) * mm]});
            skFitSpline(sketch, "E524", {"points": [v(-179.66, 232.46) * mm, v(-184.43, 226.81) * mm, v(-187.79, 219.9) * mm, v(-189.03, 213.13) * mm]});
            skFitSpline(sketch, "E525", {"points": [v(-189.03, 213.13) * mm, v(-189.65, 209.68) * mm, v(-189.85, 203.08) * mm, v(-189.45, 199.5) * mm]});
            skFitSpline(sketch, "E526", {"points": [v(-189.45, 199.5) * mm, v(-187.5, 182.59) * mm, v(-179.5, 164.47) * mm, v(-166, 146.47) * mm]});
            skFitSpline(sketch, "E527", {"points": [v(-166, 146.47) * mm, v(-146.2, 120) * mm, v(-117.88, 93.97) * mm, v(-80.49, 67.84) * mm]});
            skFitSpline(sketch, "E528", {"points": [v(-80.49, 67.84) * mm, v(-67.79, 58.95) * mm, v(-58.87, 53.16) * mm, v(-39.7, 41.3) * mm]});
            skFitSpline(sketch, "E529", {"points": [v(-39.7, 41.3) * mm, v(-32.88, 37.1) * mm, v(-25.62, 32.59) * mm, v(-23.56, 31.32) * mm]});
            skFitSpline(sketch, "E530", {"points": [v(-23.56, 31.32) * mm, v(-21.5, 30.05) * mm, v(-18.82, 28.07) * mm, v(-17.58, 26.94) * mm]});
            skFitSpline(sketch, "E531", {"points": [v(-17.58, 26.94) * mm, v(-16.34, 25.82) * mm, v(-15.01, 24.8) * mm, v(-14.62, 24.74) * mm]});
            skFitSpline(sketch, "E532", {"points": [v(-14.62, 24.74) * mm, v(-13.52, 24.52) * mm, v(-12.25, 25.22) * mm, v(-11.71, 26.35) * mm]});
            skFitSpline(sketch, "E533", {"points": [v(-11.71, 26.35) * mm, v(-11.1, 27.65) * mm, v(-11.34, 28.84) * mm, v(-13.26, 33.4) * mm]});
            skFitSpline(sketch, "E534", {"points": [v(-13.26, 33.4) * mm, v(-15.18, 38.06) * mm, v(-15.92, 41.08) * mm, v(-15.89, 44.5) * mm]});
            skFitSpline(sketch, "E535", {"points": [v(-15.89, 44.5) * mm, v(-15.89, 48.5) * mm, v(-15.38, 49.95) * mm, v(-12.39, 54.83) * mm]});
            skFitSpline(sketch, "E536", {"points": [v(-12.39, 54.83) * mm, v(-10.5, 57.88) * mm, v(-11.03, 59.82) * mm, v(-14.56, 62.98) * mm]});
            skFitSpline(sketch, "E537", {"points": [v(-14.56, 62.98) * mm, v(-18.65, 66.68) * mm, v(-22.2, 72.27) * mm, v(-24.16, 78.2) * mm]});
            skFitSpline(sketch, "E538", {"points": [v(-24.16, 78.2) * mm, v(-25.4, 81.92) * mm, v(-26.27, 85.93) * mm, v(-27.71, 94.37) * mm]});
            skFitSpline(sketch, "E539", {"points": [v(-27.71, 94.37) * mm, v(-28.36, 98.1) * mm, v(-29.12, 102.27) * mm, v(-29.43, 103.68) * mm]});
            skFitSpline(sketch, "E540", {"points": [v(-29.43, 103.68) * mm, v(-30.4, 107.86) * mm, v(-29.83, 110.57) * mm, v(-27.57, 112.54) * mm]});
            skFitSpline(sketch, "E541", {"points": [v(-27.57, 112.54) * mm, v(-27, 113.02) * mm, v(-25.4, 113.98) * mm, v(-23.96, 114.66) * mm]});
            skFitSpline(sketch, "E542", {"points": [v(-23.96, 114.66) * mm, v(-19.2, 116.89) * mm, v(-17.92, 118.92) * mm, v(-17.5, 124.82) * mm]});
            skFitSpline(sketch, "E543", {"points": [v(-17.5, 124.82) * mm, v(-17.07, 131.03) * mm, v(-16.34, 132.95) * mm, v(-13.32, 135.83) * mm]});
            skFitSpline(sketch, "E544", {"points": [v(-13.32, 135.83) * mm, v(-12.13, 136.98) * mm, v(-10.86, 137.8) * mm, v(-9.03, 138.68) * mm]});
            skFitSpline(sketch, "E545", {"points": [v(-9.03, 138.68) * mm, v(-3.7, 141.16) * mm, v(-0.99, 143.95) * mm, v(1.02, 148.98) * mm]});
            skFitSpline(sketch, "E546", {"points": [v(1.02, 148.98) * mm, v(2.2, 152) * mm, v(2.6, 154.28) * mm, v(2.6, 158.43) * mm]});
            skFitSpline(sketch, "E547", {"points": [v(2.6, 158.43) * mm, v(2.6, 162.64) * mm, v(2.37, 164.19) * mm, v(1.07, 168.48) * mm]});
            skFitSpline(sketch, "E548", {"points": [v(1.07, 168.48) * mm, v(-0.2, 172.66) * mm, v(-0.65, 175.05) * mm, v(-0.82, 178.75) * mm]});
            skFitSpline(sketch, "E549", {"points": [v(-0.82, 178.75) * mm, v(-1.16, 186.23) * mm, v(0.54, 190.01) * mm, v(5.3, 192.44) * mm]});
            skFitSpline(sketch, "E550", {"points": [v(5.3, 192.44) * mm, v(6.15, 192.86) * mm, v(7.37, 193.37) * mm, v(7.96, 193.57) * mm]});
            skFitSpline(sketch, "E551", {"points": [v(7.96, 193.57) * mm, v(8.95, 193.88) * mm, v(9.12, 193.88) * mm, v(9.46, 193.4) * mm]});
            skFitSpline(sketch, "E552", {"points": [v(9.46, 193.4) * mm, v(10.05, 192.58) * mm, v(9.88, 191.14) * mm, v(9, 189.4) * mm]});
            skFitSpline(sketch, "E553", {"points": [v(9, 189.4) * mm, v(7.2, 185.84) * mm, v(6.89, 183.3) * mm, v(7.82, 179.68) * mm]});
            skFitSpline(sketch, "E554", {"points": [v(7.82, 179.68) * mm, v(8.41, 177.4) * mm, v(9.85, 174.01) * mm, v(10.58, 173.2) * mm]});
            skFitSpline(sketch, "E555", {"points": [v(10.58, 173.2) * mm, v(11.4, 172.29) * mm, v(12.25, 172.57) * mm, v(13.97, 174.38) * mm]});
            skFitSpline(sketch, "E556", {"points": [v(13.97, 174.38) * mm, v(14.96, 175.42) * mm, v(15.8, 176.07) * mm, v(16.17, 176.07) * mm]});
            skFitSpline(sketch, "E557", {"points": [v(16.17, 176.07) * mm, v(16.85, 176.07) * mm, v(17.87, 175.11) * mm, v(18.1, 174.24) * mm]});
            skFitSpline(sketch, "E558", {"points": [v(18.1, 174.24) * mm, v(18.18, 173.93) * mm, v(18.4, 170.37) * mm, v(18.57, 166.33) * mm]});
            skFitSpline(sketch, "E559", {"points": [v(18.57, 166.33) * mm, v(19, 156.43) * mm, v(19.7, 153.32) * mm, v(22.32, 149.63) * mm]});
            skFitSpline(sketch, "E560", {"points": [v(22.32, 149.63) * mm, v(24.39, 146.7) * mm, v(24.9, 145.25) * mm, v(25, 142) * mm]});
            skFitSpline(sketch, "E561", {"points": [v(25, 142) * mm, v(25.1, 140.09) * mm, v(24.98, 138.25) * mm, v(24.64, 136.36) * mm]});
            skFitSpline(sketch, "E562", {"points": [v(24.64, 136.36) * mm, v(24.33, 134.64) * mm, v(24.1, 131.73) * mm, v(24.05, 128.66) * mm]});
            skFitSpline(sketch, "E563", {"points": [v(24.05, 128.66) * mm, v(24.02, 125.58) * mm, v(23.68, 121.2) * mm, v(23.2, 117.06) * mm]});
            skFitSpline(sketch, "E564", {"points": [v(23.2, 117.06) * mm, v(22.32, 109.52) * mm, v(22.38, 108.42) * mm, v(23.93, 105.97) * mm]});
            skFitSpline(sketch, "E565", {"points": [v(23.93, 105.97) * mm, v(25.26, 103.88) * mm, v(27.35, 103.6) * mm, v(27.77, 105.43) * mm]});
            skFitSpline(sketch, "E566", {"points": [v(27.77, 105.43) * mm, v(28.25, 107.52) * mm, v(29.4, 111.39) * mm, v(29.78, 112.15) * mm]});
            skFitSpline(sketch, "E567", {"points": [v(29.78, 112.15) * mm, v(30.6, 113.81) * mm, v(33.25, 116.04) * mm, v(33.75, 115.53) * mm]});
            skFitSpline(sketch, "E568", {"points": [v(33.75, 115.53) * mm, v(33.87, 115.42) * mm, v(33.95, 113.61) * mm, v(33.98, 111.5) * mm]});
            skFitSpline(sketch, "E569", {"points": [v(33.98, 111.5) * mm, v(34, 107.3) * mm, v(34.32, 105.26) * mm, v(36.07, 98.15) * mm]});
            skFitSpline(sketch, "E570", {"points": [v(36.07, 98.15) * mm, v(37.56, 92.05) * mm, v(37.9, 89.63) * mm, v(37.48, 87.65) * mm]});
            skFitSpline(sketch, "E571", {"points": [v(37.48, 87.65) * mm, v(36.07, 80.74) * mm, v(26.1, 69.02) * mm, v(20.18, 67.27) * mm]});
            skFitSpline(sketch, "E572", {"points": [v(20.18, 67.27) * mm, v(18.23, 66.68) * mm, v(17, 66.74) * mm, v(15.52, 67.44) * mm]});
            skFitSpline(sketch, "E573", {"points": [v(15.52, 67.44) * mm, v(14.3, 68.06) * mm, v(12.48, 70.3) * mm, v(12.81, 70.83) * mm]});
            skFitSpline(sketch, "E574", {"points": [v(12.81, 70.83) * mm, v(12.9, 70.97) * mm, v(13.97, 71.6) * mm, v(15.21, 72.24) * mm]});
            skFitSpline(sketch, "E575", {"points": [v(15.21, 72.24) * mm, v(18.18, 73.8) * mm, v(18.68, 74.53) * mm, v(18.83, 77.35) * mm]});
            skFitSpline(sketch, "E576", {"points": [v(18.83, 77.35) * mm, v(18.94, 79.86) * mm, v(18.4, 82) * mm, v(15.97, 88.92) * mm]});
            skFitSpline(sketch, "E577", {"points": [v(15.97, 88.92) * mm, v(14.56, 92.9) * mm, v(14.48, 93.07) * mm, v(14, 92.62) * mm]});
            skFitSpline(sketch, "E578", {"points": [v(14, 92.62) * mm, v(12.53, 91.3) * mm, v(11.23, 87.2) * mm, v(11.23, 83.87) * mm]});
            skFitSpline(sketch, "E579", {"points": [v(11.23, 83.87) * mm, v(11.23, 83.08) * mm, v(11.1, 82.06) * mm, v(10.95, 81.64) * mm]});
            skFitSpline(sketch, "E580", {"points": [v(10.95, 81.64) * mm, v(10.67, 80.93) * mm, v(10.56, 80.9) * mm, v(9.26, 81.02) * mm]});
            skFitSpline(sketch, "E581", {"points": [v(9.26, 81.02) * mm, v(5.93, 81.36) * mm, v(4.46, 84.04) * mm, v(3.98, 90.75) * mm]});
            skFitSpline(sketch, "E582", {"points": [v(3.98, 90.75) * mm, v(3.73, 94.5) * mm, v(4.2, 96.85) * mm, v(6.72, 104.39) * mm]});
            skFitSpline(sketch, "E583", {"points": [v(6.72, 104.39) * mm, v(9.65, 113.13) * mm, v(10.19, 115.76) * mm, v(10.19, 121.04) * mm]});
            skFitSpline(sketch, "E584", {"points": [v(10.19, 121.04) * mm, v(10.19, 123.3) * mm, v(10.08, 125.7) * mm, v(9.9, 126.4) * mm]});
            skLineSegment(sketch, "E585", {"start": v(9.9, 126.4) * mm, "end": v(9.65, 127.67) * mm});
            skLineSegment(sketch, "E586", {"start": v(9.65, 127.67) * mm, "end": v(7.76, 123.94) * mm});
            skFitSpline(sketch, "E587", {"points": [v(7.76, 123.94) * mm, v(6.69, 121.8) * mm, v(5.45, 119.77) * mm, v(4.86, 119.2) * mm]});
            skLineSegment(sketch, "E588", {"start": v(4.86, 119.2) * mm, "end": v(3.84, 118.16) * mm});
            skLineSegment(sketch, "E589", {"start": v(3.84, 118.16) * mm, "end": v(0.9, 118.36) * mm});
            skLineSegment(sketch, "E590", {"start": v(0.9, 118.36) * mm, "end": v(-2, 118.55) * mm});
            skLineSegment(sketch, "E591", {"start": v(-2, 118.55) * mm, "end": v(-2.85, 117.74) * mm});
            skFitSpline(sketch, "E592", {"points": [v(-2.85, 117.74) * mm, v(-3.84, 116.75) * mm, v(-4.1, 115.87) * mm, v(-5.67, 108.34) * mm]});
            skFitSpline(sketch, "E593", {"points": [v(-5.67, 108.34) * mm, v(-7.68, 98.66) * mm, v(-7.79, 97.87) * mm, v(-7.79, 92.53) * mm]});
            skFitSpline(sketch, "E594", {"points": [v(-7.79, 92.53) * mm, v(-7.79, 88.27) * mm, v(-7.7, 87.26) * mm, v(-7.14, 85.2) * mm]});
            skFitSpline(sketch, "E595", {"points": [v(-7.14, 85.2) * mm, v(-5.3, 78.37) * mm, v(-1.27, 71.14) * mm, v(2.96, 67.1) * mm]});
            skFitSpline(sketch, "E596", {"points": [v(2.96, 67.1) * mm, v(5.73, 64.48) * mm, v(7.45, 63.35) * mm, v(11.91, 61.2) * mm]});
            skFitSpline(sketch, "E597", {"points": [v(11.91, 61.2) * mm, v(19.84, 57.37) * mm, v(23.45, 52.65) * mm, v(23.85, 45.54) * mm]});
            skFitSpline(sketch, "E598", {"points": [v(23.85, 45.54) * mm, v(24.1, 41.22) * mm, v(23.37, 38.2) * mm, v(20.69, 32.2) * mm]});
            skFitSpline(sketch, "E599", {"points": [v(20.69, 32.2) * mm, v(20.04, 30.73) * mm, v(19.59, 29.2) * mm, v(19.5, 28.19) * mm]});
            skFitSpline(sketch, "E600", {"points": [v(19.5, 28.19) * mm, v(19.36, 26.6) * mm, v(19.39, 26.46) * mm, v(20.2, 25.67) * mm]});
            skFitSpline(sketch, "E601", {"points": [v(20.2, 25.67) * mm, v(21.6, 24.26) * mm, v(22.75, 24.43) * mm, v(24.72, 26.3) * mm]});
            skFitSpline(sketch, "E602", {"points": [v(24.72, 26.3) * mm, v(25.71, 27.23) * mm, v(30.2, 30.22) * mm, v(36.21, 33.97) * mm]});
            skFitSpline(sketch, "E603", {"points": [v(36.21, 33.97) * mm, v(75.27, 58.33) * mm, v(90.14, 68.37) * mm, v(109.59, 83.47) * mm]});
            skFitSpline(sketch, "E604", {"points": [v(109.59, 83.47) * mm, v(128.3, 98) * mm, v(142.8, 111.1) * mm, v(155.48, 124.85) * mm]});
            skFitSpline(sketch, "E605", {"points": [v(155.48, 124.85) * mm, v(169.9, 140.54) * mm, v(176.59, 149.06) * mm, v(183.25, 160.27) * mm]});
            skFitSpline(sketch, "E606", {"points": [v(183.25, 160.27) * mm, v(192.98, 176.7) * mm, v(198.77, 196.45) * mm, v(197.53, 209.12) * mm]});
            skFitSpline(sketch, "E607", {"points": [v(197.53, 209.12) * mm, v(196.65, 218.18) * mm, v(193.97, 224.53) * mm, v(187.8, 232.1) * mm]});
            skFitSpline(sketch, "E608", {"points": [v(187.8, 232.1) * mm, v(186.78, 233.33) * mm, v(185.5, 235.22) * mm, v(184.97, 236.32) * mm]});
            skFitSpline(sketch, "E609", {"points": [v(184.97, 236.32) * mm, v(183.81, 238.67) * mm, v(181.67, 244.65) * mm, v(181.87, 244.99) * mm]});
            skFitSpline(sketch, "E610", {"points": [v(181.87, 244.99) * mm, v(182.1, 245.33) * mm, v(183.08, 245.27) * mm, v(184.94, 244.8) * mm]});
            skFitSpline(sketch, "E611", {"points": [v(184.94, 244.8) * mm, v(190.33, 243.38) * mm, v(193.5, 240.42) * mm, v(194.93, 235.45) * mm]});
            skFitSpline(sketch, "E612", {"points": [v(194.93, 235.45) * mm, v(195.27, 234.2) * mm, v(195.8, 232.37) * mm, v(196.09, 231.36) * mm]});
            skFitSpline(sketch, "E613", {"points": [v(196.09, 231.36) * mm, v(196.8, 228.99) * mm, v(197.53, 228.25) * mm, v(200.27, 227.3) * mm]});
            skFitSpline(sketch, "E614", {"points": [v(200.27, 227.3) * mm, v(204.7, 225.71) * mm, v(206.76, 223.4) * mm, v(207.55, 219) * mm]});
            skFitSpline(sketch, "E615", {"points": [v(207.55, 219) * mm, v(207.77, 217.81) * mm, v(208.03, 214.73) * mm, v(208.11, 212.14) * mm]});
            skFitSpline(sketch, "E616", {"points": [v(208.11, 212.14) * mm, v(208.28, 208.24) * mm, v(208.4, 207.26) * mm, v(208.85, 206.55) * mm]});
            skFitSpline(sketch, "E617", {"points": [v(208.85, 206.55) * mm, v(209.47, 205.5) * mm, v(210.06, 205.22) * mm, v(210.62, 205.7) * mm]});
            skFitSpline(sketch, "E618", {"points": [v(210.62, 205.7) * mm, v(211.36, 206.32) * mm, v(214.12, 210.1) * mm, v(215.36, 212.25) * mm]});
            skFitSpline(sketch, "E619", {"points": [v(215.36, 212.25) * mm, v(217.45, 215.8) * mm, v(217.54, 216.09) * mm, v(217.2, 220.07) * mm]});
            skFitSpline(sketch, "E620", {"points": [v(217.2, 220.07) * mm, v(216.7, 225.85) * mm, v(217.4, 228.3) * mm, v(220.47, 231.61) * mm]});
            skFitSpline(sketch, "E621", {"points": [v(220.47, 231.61) * mm, v(222.84, 234.15) * mm, v(222.84, 234.63) * mm, v(220.25, 239.6) * mm]});
            skFitSpline(sketch, "E622", {"points": [v(220.25, 239.6) * mm, v(218.64, 242.73) * mm, v(218.36, 243.47) * mm, v(218.5, 244.31) * mm]});
            skFitSpline(sketch, "E623", {"points": [v(218.5, 244.31) * mm, v(218.67, 245.5) * mm, v(219.4, 246.34) * mm, v(220.22, 246.34) * mm]});
            skFitSpline(sketch, "E624", {"points": [v(220.22, 246.34) * mm, v(220.61, 246.34) * mm, v(221.86, 245.44) * mm, v(223.52, 243.92) * mm]});
            skFitSpline(sketch, "E625", {"points": [v(223.52, 243.92) * mm, v(226.03, 241.66) * mm, v(226.26, 241.38) * mm, v(226.94, 239.49) * mm]});
            skFitSpline(sketch, "E626", {"points": [v(226.94, 239.49) * mm, v(227.33, 238.36) * mm, v(228.1, 236.44) * mm, v(228.66, 235.17) * mm]});
            skFitSpline(sketch, "E627", {"points": [v(228.66, 235.17) * mm, v(230.15, 231.8) * mm, v(230.4, 230.2) * mm, v(229.98, 226.73) * mm]});
            skFitSpline(sketch, "E628", {"points": [v(229.98, 226.73) * mm, v(229.48, 222.47) * mm, v(230.15, 220.66) * mm, v(232.24, 220.66) * mm]});
            skFitSpline(sketch, "E629", {"points": [v(232.24, 220.66) * mm, v(233.06, 220.66) * mm, v(233.37, 221.17) * mm, v(233.94, 223.62) * mm]});
            skFitSpline(sketch, "E630", {"points": [v(233.94, 223.62) * mm, v(234.75, 227.15) * mm, v(236.5, 228.62) * mm, v(239.86, 228.6) * mm]});
            skFitSpline(sketch, "E631", {"points": [v(239.86, 228.6) * mm, v(241.98, 228.6) * mm, v(242.94, 228.14) * mm, v(242.94, 227.15) * mm]});
            skFitSpline(sketch, "E632", {"points": [v(242.94, 227.15) * mm, v(242.94, 226.1) * mm, v(241.98, 224.42) * mm, v(240.45, 222.78) * mm]});
            skFitSpline(sketch, "E633", {"points": [v(240.45, 222.78) * mm, v(239.6, 221.85) * mm, v(238.5, 220.3) * mm, v(238.06, 219.3) * mm]});
            skFitSpline(sketch, "E634", {"points": [v(238.06, 219.3) * mm, v(236.95, 216.94) * mm, v(237.04, 215.02) * mm, v(238.4, 212.42) * mm]});
            skFitSpline(sketch, "E635", {"points": [v(238.4, 212.42) * mm, v(239.33, 210.7) * mm, v(239.33, 210.56) * mm, v(239.18, 208.19) * mm]});
            skLineSegment(sketch, "E636", {"start": v(239.18, 208.19) * mm, "end": v(239.02, 205.7) * mm});
            skLineSegment(sketch, "E637", {"start": v(239.02, 205.7) * mm, "end": v(236.05, 201.75) * mm});
            skFitSpline(sketch, "E638", {"points": [v(236.05, 201.75) * mm, v(227.3, 190.13) * mm, v(221.38, 179.37) * mm, v(216.95, 166.98) * mm]});
            skFitSpline(sketch, "E639", {"points": [v(216.95, 166.98) * mm, v(216.35, 165.29) * mm, v(215.84, 163.7) * mm, v(215.84, 163.48) * mm]});
            skFitSpline(sketch, "E640", {"points": [v(215.84, 163.48) * mm, v(215.84, 163.26) * mm, v(216.13, 163.09) * mm, v(216.58, 163.09) * mm]});
            skFitSpline(sketch, "E641", {"points": [v(216.58, 163.09) * mm, v(218.1, 163.09) * mm, v(222.87, 168.03) * mm, v(226.34, 173.22) * mm]});
            skFitSpline(sketch, "E642", {"points": [v(226.34, 173.22) * mm, v(229.73, 178.3) * mm, v(232.1, 183.72) * mm, v(234.64, 192.3) * mm]});
            skFitSpline(sketch, "E643", {"points": [v(234.64, 192.3) * mm, v(235.26, 194.39) * mm, v(235.57, 195.04) * mm, v(236.56, 196.02) * mm]});
            skFitSpline(sketch, "E644", {"points": [v(236.56, 196.02) * mm, v(237.75, 197.2) * mm, v(238.9, 197.72) * mm, v(239.72, 197.4) * mm]});
            skFitSpline(sketch, "E645", {"points": [v(239.72, 197.4) * mm, v(240.09, 197.27) * mm, v(240.12, 196.56) * mm, v(239.95, 191.62) * mm]});
            skLineSegment(sketch, "E646", {"start": v(239.95, 191.62) * mm, "end": v(239.75, 186) * mm});
            skLineSegment(sketch, "E647", {"start": v(239.75, 186) * mm, "end": v(240.51, 185.52) * mm});
            skFitSpline(sketch, "E648", {"points": [v(240.51, 185.52) * mm, v(241.56, 184.85) * mm, v(242.71, 185.13) * mm, v(244.38, 186.51) * mm]});
            skFitSpline(sketch, "E649", {"points": [v(244.38, 186.51) * mm, v(246.24, 188.1) * mm, v(247.06, 189.9) * mm, v(247.57, 193.6) * mm]});
            skFitSpline(sketch, "E650", {"points": [v(247.57, 193.6) * mm, v(247.99, 196.7) * mm, v(248.38, 197.86) * mm, v(249.37, 198.73) * mm]});
            skFitSpline(sketch, "E651", {"points": [v(249.37, 198.73) * mm, v(250.16, 199.44) * mm, v(250.9, 199.16) * mm, v(252, 197.77) * mm]});
            skLineSegment(sketch, "E652", {"start": v(252, 197.77) * mm, "end": v(252.9, 196.64) * mm});
            skLineSegment(sketch, "E653", {"start": v(252.9, 196.64) * mm, "end": v(252.56, 193.62) * mm});
            skFitSpline(sketch, "E654", {"points": [v(252.56, 193.62) * mm, v(251.8, 186.63) * mm, v(251.4, 180.9) * mm, v(251.12, 173.14) * mm]});
            skFitSpline(sketch, "E655", {"points": [v(251.12, 173.14) * mm, v(250.95, 168.62) * mm, v(250.7, 164.08) * mm, v(250.53, 163.03) * mm]});
            skFitSpline(sketch, "E656", {"points": [v(250.53, 163.03) * mm, v(250.08, 160.1) * mm, v(248.9, 157.98) * mm, v(246.35, 155.41) * mm]});
            skFitSpline(sketch, "E657", {"points": [v(246.35, 155.41) * mm, v(244.4, 153.46) * mm, v(243.73, 153.01) * mm, v(240.88, 151.66) * mm]});
            skFitSpline(sketch, "E658", {"points": [v(240.88, 151.66) * mm, v(239.1, 150.81) * mm, v(237.43, 149.85) * mm, v(237.18, 149.49) * mm]});
            skFitSpline(sketch, "E659", {"points": [v(237.18, 149.49) * mm, v(236.33, 148.27) * mm, v(236.87, 145.42) * mm, v(238.08, 144.77) * mm]});
            skFitSpline(sketch, "E660", {"points": [v(238.08, 144.77) * mm, v(238.42, 144.6) * mm, v(239.52, 144.46) * mm, v(240.6, 144.43) * mm]});
            skFitSpline(sketch, "E661", {"points": [v(240.6, 144.43) * mm, v(242.88, 144.43) * mm, v(246.78, 143.84) * mm, v(247.2, 143.42) * mm]});
            skFitSpline(sketch, "E662", {"points": [v(247.2, 143.42) * mm, v(247.7, 142.9) * mm, v(246.27, 141.58) * mm, v(244.1, 140.6) * mm]});
            skFitSpline(sketch, "E663", {"points": [v(244.1, 140.6) * mm, v(239.04, 138.3) * mm, v(238.96, 137.63) * mm, v(243.05, 132.75) * mm]});
            skFitSpline(sketch, "E664", {"points": [v(243.05, 132.75) * mm, v(246.32, 128.88) * mm, v(247.2, 126.31) * mm, v(246.18, 123.69) * mm]});
            skFitSpline(sketch, "E665", {"points": [v(246.18, 123.69) * mm, v(245.48, 121.83) * mm, v(244.1, 120.42) * mm, v(241.58, 118.95) * mm]});
            skFitSpline(sketch, "E666", {"points": [v(241.58, 118.95) * mm, v(238.03, 116.92) * mm, v(237.12, 115.56) * mm, v(236.73, 111.92) * mm]});
            skFitSpline(sketch, "E667", {"points": [v(236.73, 111.92) * mm, v(236.45, 109.18) * mm, v(236.1, 108.2) * mm, v(235.1, 107.12) * mm]});
            skFitSpline(sketch, "E668", {"points": [v(235.1, 107.12) * mm, v(233.51, 105.43) * mm, v(232.75, 105.2) * mm, v(226.48, 104.64) * mm]});
            skFitSpline(sketch, "E669", {"points": [v(226.48, 104.64) * mm, v(222.59, 104.27) * mm, v(222.05, 104.05) * mm, v(222.05, 102.72) * mm]});
            skFitSpline(sketch, "E670", {"points": [v(222.05, 102.72) * mm, v(222.05, 101.45) * mm, v(223.01, 100.55) * mm, v(225.24, 99.7) * mm]});
            skFitSpline(sketch, "E671", {"points": [v(225.24, 99.7) * mm, v(228.4, 98.52) * mm, v(231.03, 97.13) * mm, v(233.6, 95.27) * mm]});
            skFitSpline(sketch, "E672", {"points": [v(233.6, 95.27) * mm, v(235.74, 93.75) * mm, v(236.16, 93.55) * mm, v(237.6, 93.44) * mm]});
            skFitSpline(sketch, "E673", {"points": [v(237.6, 93.44) * mm, v(239.72, 93.27) * mm, v(241.24, 93.8) * mm, v(245.2, 96.09) * mm]});
            skFitSpline(sketch, "E674", {"points": [v(245.2, 96.09) * mm, v(246.97, 97.08) * mm, v(248.58, 97.84) * mm, v(248.8, 97.75) * mm]});
            skFitSpline(sketch, "E675", {"points": [v(248.8, 97.75) * mm, v(249.15, 97.64) * mm, v(249.18, 97.25) * mm, v(249.03, 95.86) * mm]});
            skFitSpline(sketch, "E676", {"points": [v(249.03, 95.86) * mm, v(248.58, 92.05) * mm, v(246.92, 89.32) * mm, v(242.63, 85.48) * mm]});
            skFitSpline(sketch, "E677", {"points": [v(242.63, 85.48) * mm, v(241.16, 84.18) * mm, v(239.21, 82.32) * mm, v(238.28, 81.36) * mm]});
            skFitSpline(sketch, "E678", {"points": [v(238.28, 81.36) * mm, v(237.35, 80.43) * mm, v(235.8, 79.13) * mm, v(234.84, 78.48) * mm]});
            skFitSpline(sketch, "E679", {"points": [v(234.84, 78.48) * mm, v(232.44, 76.84) * mm, v(232.02, 75.94) * mm, v(232.92, 74.19) * mm]});
            skFitSpline(sketch, "E680", {"points": [v(232.92, 74.19) * mm, v(233.57, 72.92) * mm, v(235.32, 72.41) * mm, v(239.21, 72.38) * mm]});
            skFitSpline(sketch, "E681", {"points": [v(239.21, 72.38) * mm, v(241.02, 72.35) * mm, v(242.71, 72.41) * mm, v(242.94, 72.5) * mm]});
            skFitSpline(sketch, "E682", {"points": [v(242.94, 72.5) * mm, v(243.53, 72.7) * mm, v(243.36, 70.8) * mm, v(242.71, 70.2) * mm]});
            skFitSpline(sketch, "E683", {"points": [v(242.71, 70.2) * mm, v(241.92, 69.5) * mm, v(232.67, 65.72) * mm, v(230.6, 65.3) * mm]});
            skFitSpline(sketch, "E684", {"points": [v(230.6, 65.3) * mm, v(228.15, 64.76) * mm, v(226.6, 64.76) * mm, v(223.83, 65.3) * mm]});
            skFitSpline(sketch, "E685", {"points": [v(223.83, 65.3) * mm, v(217.11, 66.6) * mm, v(209.16, 67.05) * mm, v(201.76, 66.6) * mm]});
            skFitSpline(sketch, "E686", {"points": [v(201.76, 66.6) * mm, v(191.97, 65.95) * mm, v(189.77, 65.35) * mm, v(188.9, 63.04) * mm]});
            skFitSpline(sketch, "E687", {"points": [v(188.9, 63.04) * mm, v(187.93, 60.56) * mm, v(188.86, 58.02) * mm, v(191.04, 57.14) * mm]});
            skFitSpline(sketch, "E688", {"points": [v(191.04, 57.14) * mm, v(196.15, 55.08) * mm, v(204.84, 56.4) * mm, v(212.1, 60.39) * mm]});
            skFitSpline(sketch, "E689", {"points": [v(212.1, 60.39) * mm, v(214.43, 61.66) * mm, v(215.22, 61.74) * mm, v(216.07, 60.84) * mm]});
            skFitSpline(sketch, "E690", {"points": [v(216.07, 60.84) * mm, v(217.31, 59.51) * mm, v(217.11, 59.12) * mm, v(211.84, 53.2) * mm]});
            skFitSpline(sketch, "E691", {"points": [v(211.84, 53.2) * mm, v(210.06, 51.16) * mm, v(209.33, 50.06) * mm, v(207.72, 46.73) * mm]});
            skFitSpline(sketch, "E692", {"points": [v(207.72, 46.73) * mm, v(206.64, 44.53) * mm, v(205.18, 41.99) * mm, v(204.44, 41.11) * mm]});
            skFitSpline(sketch, "E693", {"points": [v(204.44, 41.11) * mm, v(202.83, 39.14) * mm, v(200.35, 37.8) * mm, v(197.84, 37.58) * mm]});
            skLineSegment(sketch, "E694", {"start": v(197.84, 37.58) * mm, "end": v(196.15, 37.41) * mm});
            skLineSegment(sketch, "E695", {"start": v(196.15, 37.41) * mm, "end": v(196.17, 35.24) * mm});
            skFitSpline(sketch, "E696", {"points": [v(196.17, 35.24) * mm, v(196.23, 33.4) * mm, v(196.12, 32.9) * mm, v(195.64, 32.22) * mm]});
            skFitSpline(sketch, "E697", {"points": [v(195.64, 32.22) * mm, v(194.8, 31.04) * mm, v(193.4, 30.5) * mm, v(190.73, 30.3) * mm]});
            skFitSpline(sketch, "E698", {"points": [v(190.73, 30.3) * mm, v(187.88, 30.1) * mm, v(187, 29.85) * mm, v(184.38, 28.52) * mm]});
            skFitSpline(sketch, "E699", {"points": [v(184.38, 28.52) * mm, v(181.02, 26.86) * mm, v(179.01, 26.21) * mm, v(177.12, 26.21) * mm]});
            skFitSpline(sketch, "E700", {"points": [v(177.12, 26.21) * mm, v(174.8, 26.21) * mm, v(173.29, 26.7) * mm, v(172.8, 27.6) * mm]});
            skFitSpline(sketch, "E701", {"points": [v(172.8, 27.6) * mm, v(171.82, 29.51) * mm, v(169.93, 30.56) * mm, v(165.47, 31.69) * mm]});
            skFitSpline(sketch, "E702", {"points": [v(165.47, 31.69) * mm, v(161.1, 32.79) * mm, v(158.24, 33.1) * mm, v(153.05, 33.07) * mm]});
            skFitSpline(sketch, "E703", {"points": [v(153.05, 33.07) * mm, v(148.05, 33.07) * mm, v(143.65, 32.5) * mm, v(139.02, 31.32) * mm]});
            skFitSpline(sketch, "E704", {"points": [v(139.02, 31.32) * mm, v(133.5, 29.88) * mm, v(131.3, 27.37) * mm, v(131.35, 22.49) * mm]});
            skFitSpline(sketch, "E705", {"points": [v(131.35, 22.49) * mm, v(131.38, 21.19) * mm, v(131.57, 20.23) * mm, v(132.02, 19.32) * mm]});
            skFitSpline(sketch, "E706", {"points": [v(132.02, 19.32) * mm, v(133.2, 16.84) * mm, v(135.16, 16.56) * mm, v(138.74, 18.3) * mm]});
            skFitSpline(sketch, "E707", {"points": [v(138.74, 18.3) * mm, v(140.01, 18.9) * mm, v(141.7, 19.6) * mm, v(142.52, 19.86) * mm]});
            skFitSpline(sketch, "E708", {"points": [v(142.52, 19.86) * mm, v(145.83, 20.82) * mm, v(149.44, 20.09) * mm, v(153.1, 17.69) * mm]});
            skFitSpline(sketch, "E709", {"points": [v(153.1, 17.69) * mm, v(155.56, 16.05) * mm, v(155.79, 15.94) * mm, v(158.67, 14.9) * mm]});
            skFitSpline(sketch, "E710", {"points": [v(158.67, 14.9) * mm, v(160.9, 14.1) * mm, v(163.77, 12.33) * mm, v(164.7, 11.2) * mm]});
            skFitSpline(sketch, "E711", {"points": [v(164.7, 11.2) * mm, v(165.33, 10.43) * mm, v(164.62, 10.32) * mm, v(162.56, 10.86) * mm]});
            skFitSpline(sketch, "E712", {"points": [v(162.56, 10.86) * mm, v(159.74, 11.6) * mm, v(154.83, 11.53) * mm, v(151.95, 10.74) * mm]});
            skFitSpline(sketch, "E713", {"points": [v(151.95, 10.74) * mm, v(147.89, 9.59) * mm, v(143.9, 7.27) * mm, v(138.04, 2.73) * mm]});
            skFitSpline(sketch, "E714", {"points": [v(138.04, 2.73) * mm, v(135.04, 0.36) * mm, v(134.28, -0.52) * mm, v(132.98, -3.28) * mm]});
            skFitSpline(sketch, "E715", {"points": [v(132.98, -3.28) * mm, v(131.26, -6.8) * mm, v(127.65, -9.72) * mm, v(123.95, -10.48) * mm]});
            skFitSpline(sketch, "E716", {"points": [v(123.95, -10.48) * mm, v(122.43, -10.79) * mm, v(114.56, -10.7) * mm, v(110.69, -10.3) * mm]});
            skFitSpline(sketch, "E717", {"points": [v(110.69, -10.3) * mm, v(108.43, -10.11) * mm, v(107.47, -10.6) * mm, v(104.25, -13.55) * mm]});
            skFitSpline(sketch, "E718", {"points": [v(104.25, -13.55) * mm, v(102.93, -14.8) * mm, v(101.57, -15.9) * mm, v(101.23, -15.98) * mm]});
            skFitSpline(sketch, "E719", {"points": [v(101.23, -15.98) * mm, v(100.7, -16.15) * mm, v(100.64, -16.35) * mm, v(100.75, -17.7) * mm]});
            skFitSpline(sketch, "E720", {"points": [v(100.75, -17.7) * mm, v(100.98, -20.5) * mm, v(102.25, -21.06) * mm, v(106.06, -20.05) * mm]});
            skFitSpline(sketch, "E721", {"points": [v(106.06, -20.05) * mm, v(107.84, -19.57) * mm, v(109.3, -19.4) * mm, v(111.7, -19.4) * mm]});
            skFitSpline(sketch, "E722", {"points": [v(111.7, -19.4) * mm, v(116.73, -19.37) * mm, v(118.56, -20.22) * mm, v(121.19, -23.91) * mm]});
            skFitSpline(sketch, "E723", {"points": [v(121.19, -23.91) * mm, v(124.07, -27.92) * mm, v(122.8, -30.52) * mm, v(118, -30.52) * mm]});
            skFitSpline(sketch, "E724", {"points": [v(118, -30.52) * mm, v(115.66, -30.52) * mm, v(114.22, -30.88) * mm, v(113.51, -31.67) * mm]});
            skFitSpline(sketch, "E725", {"points": [v(113.51, -31.67) * mm, v(113.06, -32.18) * mm, v(112.97, -32.72) * mm, v(112.97, -35.6) * mm]});
            skFitSpline(sketch, "E726", {"points": [v(112.97, -35.6) * mm, v(112.97, -38.84) * mm, v(112.95, -38.95) * mm, v(112.13, -40.17) * mm]});
            skFitSpline(sketch, "E727", {"points": [v(112.13, -40.17) * mm, v(111.08, -41.64) * mm, v(109.56, -42.54) * mm, v(107.47, -42.93) * mm]});
            skFitSpline(sketch, "E728", {"points": [v(107.47, -42.93) * mm, v(101.77, -43.98) * mm, v(99.8, -45.2) * mm, v(95.9, -49.99) * mm]});
            skFitSpline(sketch, "E729", {"points": [v(95.9, -49.99) * mm, v(89.63, -57.72) * mm, v(85.66, -59.13) * mm, v(79.02, -56) * mm]});
            skFitSpline(sketch, "E730", {"points": [v(79.02, -56) * mm, v(77.9, -55.46) * mm, v(75.92, -54.22) * mm, v(74.62, -53.26) * mm]});
            skFitSpline(sketch, "E731", {"points": [v(74.62, -53.26) * mm, v(73.35, -52.28) * mm, v(72.02, -51.34) * mm, v(71.71, -51.15) * mm]});
            skFitSpline(sketch, "E732", {"points": [v(71.71, -51.15) * mm, v(70.25, -50.38) * mm, v(69.15, -51.12) * mm, v(68.38, -53.38) * mm]});
            skFitSpline(sketch, "E733", {"points": [v(68.38, -53.38) * mm, v(67.65, -55.58) * mm, v(67.23, -55.8) * mm, v(64.49, -55.4) * mm]});
            skFitSpline(sketch, "E734", {"points": [v(64.49, -55.4) * mm, v(61.7, -55.01) * mm, v(59.78, -54.98) * mm, v(58.84, -55.32) * mm]});
            skFitSpline(sketch, "E735", {"points": [v(58.84, -55.32) * mm, v(58.48, -55.46) * mm, v(57.3, -56.45) * mm, v(56.2, -57.52) * mm]});
            skFitSpline(sketch, "E736", {"points": [v(56.2, -57.52) * mm, v(53.76, -59.95) * mm, v(52.1, -60.8) * mm, v(49.53, -60.94) * mm]});
            skFitSpline(sketch, "E737", {"points": [v(49.53, -60.94) * mm, v(47.05, -61.08) * mm, v(45.41, -60.54) * mm, v(42, -58.46) * mm]});
            skFitSpline(sketch, "E738", {"points": [v(42, -58.46) * mm, v(37.11, -55.46) * mm, v(34.52, -54.62) * mm, v(30.82, -54.84) * mm]});
            skFitSpline(sketch, "E739", {"points": [v(30.82, -54.84) * mm, v(28.2, -55.01) * mm, v(25.97, -55.75) * mm, v(23.23, -57.38) * mm]});
            skFitSpline(sketch, "E740", {"points": [v(23.23, -57.38) * mm, v(18, -60.46) * mm, v(16.96, -61) * mm, v(14.54, -61.79) * mm]});
            skFitSpline(sketch, "E741", {"points": [v(14.54, -61.79) * mm, v(13.1, -62.27) * mm, v(10.78, -62.86) * mm, v(9.43, -63.11) * mm]});
            skFitSpline(sketch, "E742", {"points": [v(9.43, -63.11) * mm, v(6.75, -63.56) * mm, v(1.72, -63.62) * mm, v(-1.01, -63.23) * mm]});
            skFitSpline(sketch, "E743", {"points": [v(5.25, 4.11) * mm, v(6.55, 8.15) * mm, v(7.11, 10.58) * mm, v(8.55, 18.45) * mm]});
            skFitSpline(sketch, "E744", {"points": [v(8.55, 18.45) * mm, v(9.29, 22.32) * mm, v(10.1, 26.52) * mm, v(10.42, 27.76) * mm]});
            skFitSpline(sketch, "E745", {"points": [v(10.42, 27.76) * mm, v(11.37, 31.83) * mm, v(11.1, 33.04) * mm, v(8.78, 34.65) * mm]});
            skFitSpline(sketch, "E746", {"points": [v(8.78, 34.65) * mm, v(8.04, 35.19) * mm, v(6.83, 36.17) * mm, v(6.1, 36.85) * mm]});
            skFitSpline(sketch, "E747", {"points": [v(6.1, 36.85) * mm, v(4.18, 38.6) * mm, v(3.1, 38.49) * mm, v(1.21, 36.4) * mm]});
            skFitSpline(sketch, "E748", {"points": [v(1.21, 36.4) * mm, v(0.68, 35.8) * mm, v(-0.25, 34.99) * mm, v(-0.85, 34.6) * mm]});
            skFitSpline(sketch, "E749", {"points": [v(-0.85, 34.6) * mm, v(-2.23, 33.6) * mm, v(-2.93, 32.4) * mm, v(-2.9, 30.92) * mm]});
            skFitSpline(sketch, "E750", {"points": [v(-2.9, 30.92) * mm, v(-2.9, 30.27) * mm, v(-2.4, 27.57) * mm, v(-1.78, 24.94) * mm]});
            skFitSpline(sketch, "E751", {"points": [v(-1.78, 24.94) * mm, v(-1.16, 22.29) * mm, v(0.14, 15.9) * mm, v(1.13, 10.74) * mm]});
            skLineSegment(sketch, "E752", {"start": v(1.13, 10.74) * mm, "end": v(2.9, 1.37) * mm});
            skLineSegment(sketch, "E753", {"start": v(2.9, 1.37) * mm, "end": v(3.64, 1.37) * mm});
            skFitSpline(sketch, "E754", {"points": [v(3.64, 1.37) * mm, v(4.32, 1.37) * mm, v(4.43, 1.57) * mm, v(5.25, 4.11) * mm]});
            skSolve(sketch);
        }
        {
            var Q0;
            Q0 = qSketchRegion(id + "F0", true);
            var Q1;
            Q1=makeQuery(id+"F0.imprint","IMPRINT",FACE,{"disambiguationData":[TD([[makeQuery(id+"F0.imprint","IMPRINT",EDGE,{"derivedFrom":sQuery(id+"F0.wireOp",EDGE,"E383")}),-1.0]])]});
            var Q2;
            Q2=makeQuery(id+"F0.imprint","IMPRINT",FACE,{"disambiguationData":[TD([[makeQuery(id+"F0.imprint","IMPRINT",EDGE,{"derivedFrom":sQuery(id+"F0.wireOp",EDGE,"E223")}),-1.0]])]});
            var Q3;
            Q3=makeQuery(id+"F0.imprint","IMPRINT",FACE,{"disambiguationData":[TD([[makeQuery(id+"F0.imprint","IMPRINT",EDGE,{"derivedFrom":sQuery(id+"F0.wireOp",EDGE,"E244")}),-1.0]])]});
            var Q4;
            Q4=makeQuery(id+"F0.imprint","IMPRINT",FACE,{"disambiguationData":[TD([[makeQuery(id+"F0.imprint","IMPRINT",EDGE,{"derivedFrom":sQuery(id+"F0.wireOp",EDGE,"E197")}),-1.0]])]});
            var Q5;
            Q5=makeQuery(id+"F0.imprint","IMPRINT",FACE,{"disambiguationData":[TD([[makeQuery(id+"F0.imprint","IMPRINT",EDGE,{"derivedFrom":sQuery(id+"F0.wireOp",EDGE,"E170")}),-1.0]])]});
            var Q6;
            Q6=makeQuery(id+"F0.imprint","IMPRINT",FACE,{"disambiguationData":[TD([[makeQuery(id+"F0.imprint","IMPRINT",EDGE,{"derivedFrom":sQuery(id+"F0.wireOp",EDGE,"E743")}),1.0]])]});
            var Q7;
            Q7=makeQuery(id+"F0.imprint","IMPRINT",FACE,{"disambiguationData":[TD([[makeQuery(id+"F0.imprint","IMPRINT",EDGE,{"derivedFrom":sQuery(id+"F0.wireOp",EDGE,"E371")}),-1.0]])]});
            extrude(context, id + "F1", {"entities" : qUnion([Q0, Q1, Q2, Q3, Q4, Q5, Q6, Q7]), "depth" : 20 * mm});
        }
        {
            var Q0;
            Q0=makeQuery(id+"F0.imprint","IMPRINT",FACE,{"disambiguationData":[TD([[makeQuery(id+"F0.imprint","IMPRINT",EDGE,{"derivedFrom":sQuery(id+"F0.wireOp",EDGE,"E383")}),-1.0]])]});
            var Q1;
            Q1=makeQuery(id+"F0.imprint","IMPRINT",FACE,{"disambiguationData":[TD([[makeQuery(id+"F0.imprint","IMPRINT",EDGE,{"derivedFrom":sQuery(id+"F0.wireOp",EDGE,"E244")}),-1.0]])]});
            var Q2;
            Q2=makeQuery(id+"F0.imprint","IMPRINT",FACE,{"disambiguationData":[TD([[makeQuery(id+"F0.imprint","IMPRINT",EDGE,{"derivedFrom":sQuery(id+"F0.wireOp",EDGE,"E371")}),-1.0]])]});
            var Q3;
            Q3=makeQuery(id+"F0.imprint","IMPRINT",FACE,{"disambiguationData":[TD([[makeQuery(id+"F0.imprint","IMPRINT",EDGE,{"derivedFrom":sQuery(id+"F0.wireOp",EDGE,"E197")}),-1.0]])]});
            var Q4;
            Q4=makeQuery(id+"F0.imprint","IMPRINT",FACE,{"disambiguationData":[TD([[makeQuery(id+"F0.imprint","IMPRINT",EDGE,{"derivedFrom":sQuery(id+"F0.wireOp",EDGE,"E170")}),-1.0]])]});
            var Q5;
            Q5=makeQuery(id+"F0.imprint","IMPRINT",FACE,{"disambiguationData":[TD([[makeQuery(id+"F0.imprint","IMPRINT",EDGE,{"derivedFrom":sQuery(id+"F0.wireOp",EDGE,"E223")}),-1.0]])]});
            extrude(context, id + "F2", {"entities" : qUnion([Q0, Q1, Q2, Q3, Q4, Q5]), "operationType" : NewBodyOperationType.ADD, "depth" : 30 * mm});
        }
    });
